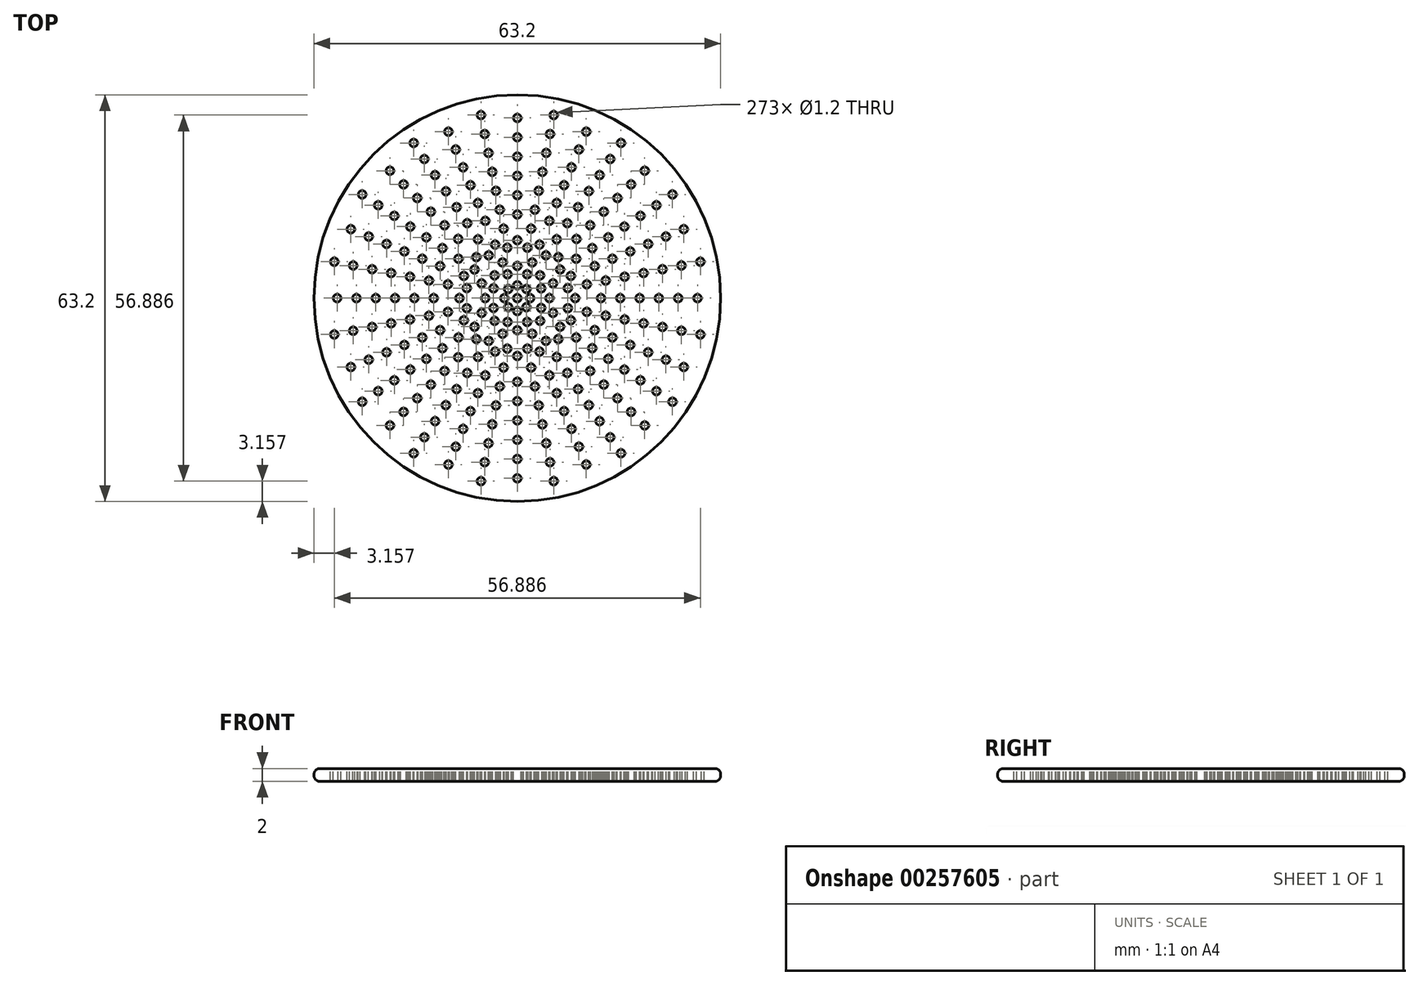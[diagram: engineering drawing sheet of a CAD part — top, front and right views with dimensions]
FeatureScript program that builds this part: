
annotation { "Feature Type Name" : "Feature", "Feature Type Description" : "" }
export const myFeature = defineFeature(function(context is Context, id is Id, definition is map)
    precondition{}
    {
        {
            var Q0;
            Q0=qCreatedBy(makeId("Front.planeOp"),FACE);
            var sketch = newSketch(context, id + "F0", { "sketchPlane" : qUnion([Q0])});
            skLineSegment(sketch, "E0", {"start": v(0, 0) * mm, "end": v(31.6, 0) * mm});
            skLineSegment(sketch, "E1", {"start": v(31.6, 0) * mm, "end": v(31.6, 2) * mm});
            skLineSegment(sketch, "E2", {"start": v(31.6, 2) * mm, "end": v(0, 2) * mm});
            skLineSegment(sketch, "E3", {"start": v(0, 2) * mm, "end": v(0, 0) * mm});
            skLineSegment(sketch, "E4", {"start": v(0, -1.67) * mm, "end": v(0, 4.38) * mm, "construction": true});
            skSolve(sketch);
        }
        {
            var Q0;
            Q0=makeQuery(id+"F0.imprint","IMPRINT",FACE,{"disambiguationData":[TD([[makeQuery(id+"F0.imprint","IMPRINT",EDGE,{"derivedFrom":sQuery(id+"F0.wireOp",EDGE,"E0")}),1.0]])]});
            var Q1;
            Q1=sQuery(id+"F0.wireOp",EDGE,"E4");
            revolve(context, id + "F1", {"entities" : qUnion([Q0]), "axis" : qUnion([Q1]), "revolveType" : RevolveType.FULL});
        }
        {
            var Q0;
            Q0=makeQuery(id+"F1.opRevolve","SWEPT_FACE",FACE,{"disambiguationData":[OSD([sQuery(id+"F0.wireOp",EDGE,"E2")])]});
            var sketch = newSketch(context, id + "F2", { "sketchPlane" : qUnion([Q0])});
            skCircle(sketch, "E5", {"center": v(0, 0) * mm, "radius": 2 * mm});
            skCircle(sketch, "E6", {"center": v(0, 0) * mm, "radius": 3 * mm});
            skCircle(sketch, "E7", {"center": v(0, 0) * mm, "radius": 4 * mm});
            skCircle(sketch, "E8", {"center": v(0, 0) * mm, "radius": 5 * mm});
            skCircle(sketch, "E9", {"center": v(0, 0) * mm, "radius": 6 * mm});
            skCircle(sketch, "E10", {"center": v(0, 0) * mm, "radius": 7 * mm});
            skCircle(sketch, "E11", {"center": v(0, 0) * mm, "radius": 8 * mm});
            skCircle(sketch, "E12", {"center": v(0, 0) * mm, "radius": 9 * mm});
            skCircle(sketch, "E13", {"center": v(0, 0) * mm, "radius": 10 * mm});
            skCircle(sketch, "E14", {"center": v(0, 0) * mm, "radius": 11 * mm});
            skCircle(sketch, "E15", {"center": v(0, 0) * mm, "radius": 12 * mm});
            skCircle(sketch, "E16", {"center": v(0, 0) * mm, "radius": 13 * mm});
            skCircle(sketch, "E17", {"center": v(0, 0) * mm, "radius": 14 * mm});
            skCircle(sketch, "E18", {"center": v(0, 0) * mm, "radius": 15 * mm});
            skCircle(sketch, "E19", {"center": v(0, 0) * mm, "radius": 16 * mm});
            skCircle(sketch, "E20", {"center": v(0, 0) * mm, "radius": 17 * mm});
            skCircle(sketch, "E21", {"center": v(0, 0) * mm, "radius": 18 * mm});
            skCircle(sketch, "E22", {"center": v(0, 0) * mm, "radius": 19 * mm});
            skCircle(sketch, "E23", {"center": v(0, 0) * mm, "radius": 20 * mm});
            skCircle(sketch, "E24", {"center": v(0, 0) * mm, "radius": 21 * mm});
            skCircle(sketch, "E25", {"center": v(0, 0) * mm, "radius": 23 * mm});
            skCircle(sketch, "E26", {"center": v(0, 0) * mm, "radius": 24 * mm});
            skCircle(sketch, "E27", {"center": v(0, 0) * mm, "radius": 22 * mm});
            skCircle(sketch, "E28", {"center": v(0, 0) * mm, "radius": 25 * mm});
            skCircle(sketch, "E29", {"center": v(0, 0) * mm, "radius": 26 * mm});
            skCircle(sketch, "E30", {"center": v(0, 0) * mm, "radius": 27 * mm});
            skCircle(sketch, "E31", {"center": v(0, 0) * mm, "radius": 28 * mm});
            skCircle(sketch, "E32", {"center": v(0, 0) * mm, "radius": 29 * mm});
            skLineSegment(sketch, "E33", {"start": v(0, 29) * mm, "end": v(0, -29) * mm});
            skLineSegment(sketch, "E34", {"start": v(-29, 0) * mm, "end": v(29, 0) * mm});
            skLineSegment(sketch, "E35", {"start": v(20.5, 20.5) * mm, "end": v(0, 0) * mm});
            skLineSegment(sketch, "E36", {"start": v(20.5, -20.5) * mm, "end": v(0, 0) * mm});
            skLineSegment(sketch, "E37", {"start": v(-20.5, -20.5) * mm, "end": v(0, 0) * mm});
            skLineSegment(sketch, "E38", {"start": v(-20.5, 20.5) * mm, "end": v(0, 0) * mm});
            skLineSegment(sketch, "E39", {"start": v(0, 0) * mm, "end": v(26.8, 11.1) * mm});
            skLineSegment(sketch, "E40", {"start": v(0, 0) * mm, "end": v(26.8, -11.1) * mm});
            skLineSegment(sketch, "E41", {"start": v(0, 0) * mm, "end": v(11.1, -26.8) * mm});
            skLineSegment(sketch, "E42", {"start": v(0, 0) * mm, "end": v(-11.1, -26.8) * mm});
            skLineSegment(sketch, "E43", {"start": v(0, 0) * mm, "end": v(-26.8, -11.1) * mm});
            skLineSegment(sketch, "E44", {"start": v(0, 0) * mm, "end": v(-26.8, 11.1) * mm});
            skLineSegment(sketch, "E45", {"start": v(0, 0) * mm, "end": v(-11.1, 26.8) * mm});
            skLineSegment(sketch, "E46", {"start": v(0, 0) * mm, "end": v(11.1, 26.8) * mm});
            skLineSegment(sketch, "E47", {"start": v(0, 0) * mm, "end": v(28.44, 5.66) * mm});
            skLineSegment(sketch, "E48", {"start": v(0, 0) * mm, "end": v(28.44, -5.66) * mm});
            skLineSegment(sketch, "E49", {"start": v(0, 0) * mm, "end": v(24.11, -16.11) * mm});
            skLineSegment(sketch, "E50", {"start": v(0, 0) * mm, "end": v(16.11, -24.11) * mm});
            skLineSegment(sketch, "E51", {"start": v(0, 0) * mm, "end": v(5.66, -28.44) * mm});
            skLineSegment(sketch, "E52", {"start": v(0, 0) * mm, "end": v(-5.66, -28.44) * mm});
            skLineSegment(sketch, "E53", {"start": v(0, 0) * mm, "end": v(-16.11, -24.11) * mm});
            skLineSegment(sketch, "E54", {"start": v(0, 0) * mm, "end": v(-24.11, -16.11) * mm});
            skLineSegment(sketch, "E55", {"start": v(0, 0) * mm, "end": v(-28.44, -5.66) * mm});
            skLineSegment(sketch, "E56", {"start": v(0, 0) * mm, "end": v(-28.44, 5.66) * mm});
            skLineSegment(sketch, "E57", {"start": v(0, 0) * mm, "end": v(-24.11, 16.11) * mm});
            skLineSegment(sketch, "E58", {"start": v(0, 0) * mm, "end": v(-16.11, 24.11) * mm});
            skLineSegment(sketch, "E59", {"start": v(0, 0) * mm, "end": v(-5.66, 28.44) * mm});
            skLineSegment(sketch, "E60", {"start": v(0, 0) * mm, "end": v(5.66, 28.44) * mm});
            skLineSegment(sketch, "E61", {"start": v(0, 0) * mm, "end": v(16.11, 24.11) * mm});
            skLineSegment(sketch, "E62", {"start": v(0, 0) * mm, "end": v(24.11, 16.11) * mm});
            skPoint(sketch, "E63", {"position": v(0, -2) * mm});
            skPoint(sketch, "E64", {"position": v(0, -3) * mm});
            skPoint(sketch, "E65", {"position": v(0, -4) * mm});
            skPoint(sketch, "E66", {"position": v(0, -5) * mm});
            skPoint(sketch, "E67", {"position": v(0, -6) * mm});
            skPoint(sketch, "E68", {"position": v(0, -7) * mm});
            skPoint(sketch, "E69", {"position": v(0, 2) * mm});
            skPoint(sketch, "E70", {"position": v(0, 3) * mm});
            skPoint(sketch, "E71", {"position": v(0.59, 2.94) * mm});
            skPoint(sketch, "E72", {"position": v(1.15, 2.77) * mm});
            skPoint(sketch, "E73", {"position": v(1.67, 2.5) * mm});
            skPoint(sketch, "E74", {"position": v(2.12, 2.12) * mm});
            skPoint(sketch, "E75", {"position": v(2.5, 1.67) * mm});
            skPoint(sketch, "E76", {"position": v(2.77, 1.15) * mm});
            skPoint(sketch, "E77", {"position": v(2.94, 0.59) * mm});
            skPoint(sketch, "E78", {"position": v(3, 0) * mm});
            skPoint(sketch, "E79", {"position": v(2.94, -0.59) * mm});
            skPoint(sketch, "E80", {"position": v(2.77, -1.15) * mm});
            skPoint(sketch, "E81", {"position": v(2.5, -1.67) * mm});
            skPoint(sketch, "E82", {"position": v(2.12, -2.12) * mm});
            skPoint(sketch, "E83", {"position": v(1.67, -2.5) * mm});
            skPoint(sketch, "E84", {"position": v(1.15, -2.77) * mm});
            skPoint(sketch, "E85", {"position": v(0.59, -2.94) * mm});
            skPoint(sketch, "E86", {"position": v(-0.59, -2.94) * mm});
            skPoint(sketch, "E87", {"position": v(-1.15, -2.77) * mm});
            skPoint(sketch, "E88", {"position": v(-1.67, -2.5) * mm});
            skPoint(sketch, "E89", {"position": v(-2.12, -2.12) * mm});
            skPoint(sketch, "E90", {"position": v(-2.5, -1.67) * mm});
            skPoint(sketch, "E91", {"position": v(-2.77, -1.15) * mm});
            skPoint(sketch, "E92", {"position": v(-2.94, -0.59) * mm});
            skPoint(sketch, "E93", {"position": v(-3, 0) * mm});
            skPoint(sketch, "E94", {"position": v(-2.94, 0.59) * mm});
            skPoint(sketch, "E95", {"position": v(-2.77, 1.15) * mm});
            skPoint(sketch, "E96", {"position": v(-2.5, 1.67) * mm});
            skPoint(sketch, "E97", {"position": v(-2.12, 2.12) * mm});
            skPoint(sketch, "E98", {"position": v(-1.67, 2.5) * mm});
            skPoint(sketch, "E99", {"position": v(-1.15, 2.77) * mm});
            skPoint(sketch, "E100", {"position": v(-0.59, 2.94) * mm});
            skPoint(sketch, "E101", {"position": v(-0.78, 3.92) * mm});
            skPoint(sketch, "E102", {"position": v(0, 4) * mm});
            skPoint(sketch, "E103", {"position": v(0.78, 3.92) * mm});
            skPoint(sketch, "E104", {"position": v(1.53, 3.7) * mm});
            skPoint(sketch, "E105", {"position": v(2.22, 3.33) * mm});
            skPoint(sketch, "E106", {"position": v(2.83, 2.83) * mm});
            skPoint(sketch, "E107", {"position": v(3.33, 2.22) * mm});
            skPoint(sketch, "E108", {"position": v(3.7, 1.53) * mm});
            skPoint(sketch, "E109", {"position": v(3.92, 0.78) * mm});
            skPoint(sketch, "E110", {"position": v(4, 0) * mm});
            skPoint(sketch, "E111", {"position": v(3.92, -0.78) * mm});
            skPoint(sketch, "E112", {"position": v(3.7, -1.53) * mm});
            skPoint(sketch, "E113", {"position": v(3.33, -2.22) * mm});
            skPoint(sketch, "E114", {"position": v(2.83, -2.83) * mm});
            skPoint(sketch, "E115", {"position": v(2.22, -3.33) * mm});
            skPoint(sketch, "E116", {"position": v(1.53, -3.7) * mm});
            skPoint(sketch, "E117", {"position": v(0.78, -3.92) * mm});
            skPoint(sketch, "E118", {"position": v(-0.78, -3.92) * mm});
            skPoint(sketch, "E119", {"position": v(-1.53, -3.7) * mm});
            skPoint(sketch, "E120", {"position": v(-2.22, -3.33) * mm});
            skPoint(sketch, "E121", {"position": v(-2.83, -2.83) * mm});
            skPoint(sketch, "E122", {"position": v(-3.33, -2.22) * mm});
            skPoint(sketch, "E123", {"position": v(-3.7, -1.53) * mm});
            skPoint(sketch, "E124", {"position": v(-3.92, -0.78) * mm});
            skPoint(sketch, "E125", {"position": v(-4, 0) * mm});
            skPoint(sketch, "E126", {"position": v(-3.92, 0.78) * mm});
            skPoint(sketch, "E127", {"position": v(-3.7, 1.53) * mm});
            skPoint(sketch, "E128", {"position": v(-3.33, 2.22) * mm});
            skPoint(sketch, "E129", {"position": v(-2.83, 2.83) * mm});
            skPoint(sketch, "E130", {"position": v(-2.22, 3.33) * mm});
            skPoint(sketch, "E131", {"position": v(-1.53, 3.7) * mm});
            skPoint(sketch, "E132", {"position": v(-0.98, 4.9) * mm});
            skPoint(sketch, "E133", {"position": v(0, 5) * mm});
            skPoint(sketch, "E134", {"position": v(0.98, 4.9) * mm});
            skPoint(sketch, "E135", {"position": v(2.78, 4.16) * mm});
            skPoint(sketch, "E136", {"position": v(1.91, 4.62) * mm});
            skPoint(sketch, "E137", {"position": v(3.54, 3.54) * mm});
            skPoint(sketch, "E138", {"position": v(4.16, 2.78) * mm});
            skPoint(sketch, "E139", {"position": v(4.62, 1.91) * mm});
            skPoint(sketch, "E140", {"position": v(4.9, 0.98) * mm});
            skPoint(sketch, "E141", {"position": v(5, 0) * mm});
            skPoint(sketch, "E142", {"position": v(4.9, -0.98) * mm});
            skPoint(sketch, "E143", {"position": v(4.62, -1.91) * mm});
            skPoint(sketch, "E144", {"position": v(4.16, -2.78) * mm});
            skPoint(sketch, "E145", {"position": v(3.54, -3.54) * mm});
            skPoint(sketch, "E146", {"position": v(2.78, -4.16) * mm});
            skPoint(sketch, "E147", {"position": v(1.91, -4.62) * mm});
            skPoint(sketch, "E148", {"position": v(0.98, -4.9) * mm});
            skPoint(sketch, "E149", {"position": v(-0.98, -4.9) * mm});
            skPoint(sketch, "E150", {"position": v(-1.91, -4.62) * mm});
            skPoint(sketch, "E151", {"position": v(-2.78, -4.16) * mm});
            skPoint(sketch, "E152", {"position": v(-3.54, -3.54) * mm});
            skPoint(sketch, "E153", {"position": v(-4.16, -2.78) * mm});
            skPoint(sketch, "E154", {"position": v(-4.62, -1.91) * mm});
            skPoint(sketch, "E155", {"position": v(-4.9, -0.98) * mm});
            skPoint(sketch, "E156", {"position": v(-5, 0) * mm});
            skPoint(sketch, "E157", {"position": v(-4.9, 0.98) * mm});
            skPoint(sketch, "E158", {"position": v(-4.62, 1.91) * mm});
            skPoint(sketch, "E159", {"position": v(-4.16, 2.78) * mm});
            skPoint(sketch, "E160", {"position": v(-3.54, 3.54) * mm});
            skPoint(sketch, "E161", {"position": v(-2.78, 4.16) * mm});
            skPoint(sketch, "E162", {"position": v(-1.91, 4.62) * mm});
            skPoint(sketch, "E163", {"position": v(0, 6) * mm});
            skPoint(sketch, "E164", {"position": v(0, 7) * mm});
            skPoint(sketch, "E165", {"position": v(0, 8) * mm});
            skPoint(sketch, "E166", {"position": v(0, 9) * mm});
            skPoint(sketch, "E167", {"position": v(0, 10) * mm});
            skPoint(sketch, "E168", {"position": v(0, 11) * mm});
            skPoint(sketch, "E169", {"position": v(0, 12) * mm});
            skPoint(sketch, "E170", {"position": v(0, 13) * mm});
            skPoint(sketch, "E171", {"position": v(0, 14) * mm});
            skPoint(sketch, "E172", {"position": v(0, 15) * mm});
            skPoint(sketch, "E173", {"position": v(0, 16) * mm});
            skPoint(sketch, "E174", {"position": v(0, 17) * mm});
            skPoint(sketch, "E175", {"position": v(0, 18) * mm});
            skPoint(sketch, "E176", {"position": v(1.17, 5.88) * mm});
            skPoint(sketch, "E177", {"position": v(2.3, 5.54) * mm});
            skPoint(sketch, "E178", {"position": v(3.33, 4.99) * mm});
            skPoint(sketch, "E179", {"position": v(4.24, 4.24) * mm});
            skPoint(sketch, "E180", {"position": v(4.99, 3.33) * mm});
            skPoint(sketch, "E181", {"position": v(5.54, 2.3) * mm});
            skPoint(sketch, "E182", {"position": v(5.88, 1.17) * mm});
            skPoint(sketch, "E183", {"position": v(6, 0) * mm});
            skPoint(sketch, "E184", {"position": v(5.88, -1.17) * mm});
            skPoint(sketch, "E185", {"position": v(5.54, -2.3) * mm});
            skPoint(sketch, "E186", {"position": v(4.99, -3.33) * mm});
            skPoint(sketch, "E187", {"position": v(4.24, -4.24) * mm});
            skPoint(sketch, "E188", {"position": v(3.33, -4.99) * mm});
            skPoint(sketch, "E189", {"position": v(2.3, -5.54) * mm});
            skPoint(sketch, "E190", {"position": v(1.17, -5.88) * mm});
            skPoint(sketch, "E191", {"position": v(-1.17, -5.88) * mm});
            skPoint(sketch, "E192", {"position": v(-2.3, -5.54) * mm});
            skPoint(sketch, "E193", {"position": v(-3.33, -4.99) * mm});
            skPoint(sketch, "E194", {"position": v(-4.24, -4.24) * mm});
            skPoint(sketch, "E195", {"position": v(-4.99, -3.33) * mm});
            skPoint(sketch, "E196", {"position": v(-5.54, -2.3) * mm});
            skPoint(sketch, "E197", {"position": v(-5.88, -1.17) * mm});
            skPoint(sketch, "E198", {"position": v(-6, 0) * mm});
            skPoint(sketch, "E199", {"position": v(-5.88, 1.17) * mm});
            skPoint(sketch, "E200", {"position": v(-5.54, 2.3) * mm});
            skPoint(sketch, "E201", {"position": v(-4.99, 3.33) * mm});
            skPoint(sketch, "E202", {"position": v(-4.24, 4.24) * mm});
            skPoint(sketch, "E203", {"position": v(-3.33, 4.99) * mm});
            skPoint(sketch, "E204", {"position": v(-2.3, 5.54) * mm});
            skPoint(sketch, "E205", {"position": v(-1.17, 5.88) * mm});
            skPoint(sketch, "E206", {"position": v(-1.37, 6.87) * mm});
            skPoint(sketch, "E207", {"position": v(1.37, 6.87) * mm});
            skPoint(sketch, "E208", {"position": v(2.68, 6.47) * mm});
            skPoint(sketch, "E209", {"position": v(3.89, 5.82) * mm});
            skPoint(sketch, "E210", {"position": v(4.95, 4.95) * mm});
            skPoint(sketch, "E211", {"position": v(5.82, 3.89) * mm});
            skPoint(sketch, "E212", {"position": v(6.47, 2.68) * mm});
            skPoint(sketch, "E213", {"position": v(6.87, 1.37) * mm});
            skPoint(sketch, "E214", {"position": v(7, 0) * mm});
            skPoint(sketch, "E215", {"position": v(6.87, -1.37) * mm});
            skPoint(sketch, "E216", {"position": v(6.47, -2.68) * mm});
            skPoint(sketch, "E217", {"position": v(5.82, -3.89) * mm});
            skPoint(sketch, "E218", {"position": v(4.95, -4.95) * mm});
            skPoint(sketch, "E219", {"position": v(3.89, -5.82) * mm});
            skPoint(sketch, "E220", {"position": v(2.68, -6.47) * mm});
            skPoint(sketch, "E221", {"position": v(1.37, -6.87) * mm});
            skPoint(sketch, "E222", {"position": v(-1.37, -6.87) * mm});
            skPoint(sketch, "E223", {"position": v(-2.68, -6.47) * mm});
            skPoint(sketch, "E224", {"position": v(-3.89, -5.82) * mm});
            skPoint(sketch, "E225", {"position": v(-4.95, -4.95) * mm});
            skPoint(sketch, "E226", {"position": v(-5.82, -3.89) * mm});
            skPoint(sketch, "E227", {"position": v(-6.47, -2.68) * mm});
            skPoint(sketch, "E228", {"position": v(-6.87, -1.37) * mm});
            skPoint(sketch, "E229", {"position": v(-7, 0) * mm});
            skPoint(sketch, "E230", {"position": v(-6.87, 1.37) * mm});
            skPoint(sketch, "E231", {"position": v(-6.47, 2.68) * mm});
            skPoint(sketch, "E232", {"position": v(-5.82, 3.89) * mm});
            skPoint(sketch, "E233", {"position": v(-4.95, 4.95) * mm});
            skPoint(sketch, "E234", {"position": v(-3.89, 5.82) * mm});
            skPoint(sketch, "E235", {"position": v(-2.68, 6.47) * mm});
            skPoint(sketch, "E236", {"position": v(-1.56, 7.85) * mm});
            skPoint(sketch, "E237", {"position": v(1.56, 7.85) * mm});
            skPoint(sketch, "E238", {"position": v(3.06, 7.4) * mm});
            skPoint(sketch, "E239", {"position": v(4.44, 6.65) * mm});
            skPoint(sketch, "E240", {"position": v(5.66, 5.66) * mm});
            skPoint(sketch, "E241", {"position": v(6.65, 4.44) * mm});
            skPoint(sketch, "E242", {"position": v(7.4, 3.06) * mm});
            skPoint(sketch, "E243", {"position": v(7.85, 1.56) * mm});
            skPoint(sketch, "E244", {"position": v(8, 0) * mm});
            skPoint(sketch, "E245", {"position": v(7.85, -1.56) * mm});
            skPoint(sketch, "E246", {"position": v(7.4, -3.06) * mm});
            skPoint(sketch, "E247", {"position": v(6.65, -4.44) * mm});
            skPoint(sketch, "E248", {"position": v(5.66, -5.66) * mm});
            skPoint(sketch, "E249", {"position": v(4.44, -6.65) * mm});
            skPoint(sketch, "E250", {"position": v(3.06, -7.4) * mm});
            skPoint(sketch, "E251", {"position": v(1.56, -7.85) * mm});
            skPoint(sketch, "E252", {"position": v(0, -8) * mm});
            skPoint(sketch, "E253", {"position": v(-1.56, -7.85) * mm});
            skPoint(sketch, "E254", {"position": v(-3.06, -7.4) * mm});
            skPoint(sketch, "E255", {"position": v(-4.44, -6.65) * mm});
            skPoint(sketch, "E256", {"position": v(-5.66, -5.66) * mm});
            skPoint(sketch, "E257", {"position": v(-6.65, -4.44) * mm});
            skPoint(sketch, "E258", {"position": v(-7.4, -3.06) * mm});
            skPoint(sketch, "E259", {"position": v(-7.85, -1.56) * mm});
            skPoint(sketch, "E260", {"position": v(-8, 0) * mm});
            skPoint(sketch, "E261", {"position": v(-7.85, 1.56) * mm});
            skPoint(sketch, "E262", {"position": v(-7.4, 3.06) * mm});
            skPoint(sketch, "E263", {"position": v(-6.65, 4.44) * mm});
            skPoint(sketch, "E264", {"position": v(-5.66, 5.66) * mm});
            skPoint(sketch, "E265", {"position": v(-4.44, 6.65) * mm});
            skPoint(sketch, "E266", {"position": v(-3.06, 7.4) * mm});
            skPoint(sketch, "E267", {"position": v(-1.76, 8.83) * mm});
            skPoint(sketch, "E268", {"position": v(1.76, 8.83) * mm});
            skPoint(sketch, "E269", {"position": v(3.44, 8.31) * mm});
            skPoint(sketch, "E270", {"position": v(5, 7.48) * mm});
            skPoint(sketch, "E271", {"position": v(6.36, 6.36) * mm});
            skPoint(sketch, "E272", {"position": v(7.48, 5) * mm});
            skPoint(sketch, "E273", {"position": v(8.31, 3.44) * mm});
            skPoint(sketch, "E274", {"position": v(8.83, 1.76) * mm});
            skPoint(sketch, "E275", {"position": v(9, 0) * mm});
            skPoint(sketch, "E276", {"position": v(8.83, -1.76) * mm});
            skPoint(sketch, "E277", {"position": v(8.31, -3.44) * mm});
            skPoint(sketch, "E278", {"position": v(7.48, -5) * mm});
            skPoint(sketch, "E279", {"position": v(6.36, -6.36) * mm});
            skPoint(sketch, "E280", {"position": v(5, -7.48) * mm});
            skPoint(sketch, "E281", {"position": v(3.44, -8.31) * mm});
            skPoint(sketch, "E282", {"position": v(1.76, -8.83) * mm});
            skPoint(sketch, "E283", {"position": v(0, -9) * mm});
            skPoint(sketch, "E284", {"position": v(-1.76, -8.83) * mm});
            skPoint(sketch, "E285", {"position": v(-3.44, -8.31) * mm});
            skPoint(sketch, "E286", {"position": v(-5, -7.48) * mm});
            skPoint(sketch, "E287", {"position": v(-6.36, -6.36) * mm});
            skPoint(sketch, "E288", {"position": v(-7.48, -5) * mm});
            skPoint(sketch, "E289", {"position": v(-8.31, -3.44) * mm});
            skPoint(sketch, "E290", {"position": v(-8.83, -1.76) * mm});
            skPoint(sketch, "E291", {"position": v(-9, 0) * mm});
            skPoint(sketch, "E292", {"position": v(-8.83, 1.76) * mm});
            skPoint(sketch, "E293", {"position": v(-8.31, 3.44) * mm});
            skPoint(sketch, "E294", {"position": v(-7.48, 5) * mm});
            skPoint(sketch, "E295", {"position": v(-6.36, 6.36) * mm});
            skPoint(sketch, "E296", {"position": v(-5, 7.48) * mm});
            skPoint(sketch, "E297", {"position": v(-3.44, 8.31) * mm});
            skPoint(sketch, "E298", {"position": v(-1.95, 9.8) * mm});
            skPoint(sketch, "E299", {"position": v(1.95, 9.8) * mm});
            skPoint(sketch, "E300", {"position": v(3.83, 9.24) * mm});
            skPoint(sketch, "E301", {"position": v(5.56, 8.31) * mm});
            skPoint(sketch, "E302", {"position": v(7.07, 7.07) * mm});
            skPoint(sketch, "E303", {"position": v(8.31, 5.56) * mm});
            skPoint(sketch, "E304", {"position": v(9.24, 3.83) * mm});
            skPoint(sketch, "E305", {"position": v(9.8, 1.95) * mm});
            skPoint(sketch, "E306", {"position": v(10, 0) * mm});
            skPoint(sketch, "E307", {"position": v(9.8, -1.95) * mm});
            skPoint(sketch, "E308", {"position": v(9.24, -3.83) * mm});
            skPoint(sketch, "E309", {"position": v(8.31, -5.56) * mm});
            skPoint(sketch, "E310", {"position": v(7.07, -7.07) * mm});
            skPoint(sketch, "E311", {"position": v(5.56, -8.31) * mm});
            skPoint(sketch, "E312", {"position": v(3.83, -9.24) * mm});
            skPoint(sketch, "E313", {"position": v(1.95, -9.8) * mm});
            skPoint(sketch, "E314", {"position": v(0, -10) * mm});
            skPoint(sketch, "E315", {"position": v(-1.95, -9.8) * mm});
            skPoint(sketch, "E316", {"position": v(-3.83, -9.24) * mm});
            skPoint(sketch, "E317", {"position": v(-5.56, -8.31) * mm});
            skPoint(sketch, "E318", {"position": v(-7.07, -7.07) * mm});
            skPoint(sketch, "E319", {"position": v(-8.31, -5.56) * mm});
            skPoint(sketch, "E320", {"position": v(-9.24, -3.83) * mm});
            skPoint(sketch, "E321", {"position": v(-9.8, -1.95) * mm});
            skPoint(sketch, "E322", {"position": v(-10, 0) * mm});
            skPoint(sketch, "E323", {"position": v(-9.8, 1.95) * mm});
            skPoint(sketch, "E324", {"position": v(-9.24, 3.83) * mm});
            skPoint(sketch, "E325", {"position": v(-8.31, 5.56) * mm});
            skPoint(sketch, "E326", {"position": v(-7.07, 7.07) * mm});
            skPoint(sketch, "E327", {"position": v(-5.56, 8.31) * mm});
            skPoint(sketch, "E328", {"position": v(-3.83, 9.24) * mm});
            skPoint(sketch, "E329", {"position": v(-2.15, 10.79) * mm});
            skPoint(sketch, "E330", {"position": v(2.15, 10.79) * mm});
            skPoint(sketch, "E331", {"position": v(4.2, 10.16) * mm});
            skPoint(sketch, "E332", {"position": v(6.11, 9.15) * mm});
            skPoint(sketch, "E333", {"position": v(7.78, 7.78) * mm});
            skPoint(sketch, "E334", {"position": v(9.15, 6.11) * mm});
            skPoint(sketch, "E335", {"position": v(10.16, 4.2) * mm});
            skPoint(sketch, "E336", {"position": v(10.79, 2.15) * mm});
            skPoint(sketch, "E337", {"position": v(11, 0) * mm});
            skPoint(sketch, "E338", {"position": v(10.79, -2.15) * mm});
            skPoint(sketch, "E339", {"position": v(10.16, -4.2) * mm});
            skPoint(sketch, "E340", {"position": v(9.15, -6.11) * mm});
            skPoint(sketch, "E341", {"position": v(7.78, -7.78) * mm});
            skPoint(sketch, "E342", {"position": v(6.11, -9.15) * mm});
            skPoint(sketch, "E343", {"position": v(4.2, -10.16) * mm});
            skPoint(sketch, "E344", {"position": v(2.15, -10.79) * mm});
            skPoint(sketch, "E345", {"position": v(0, -11) * mm});
            skPoint(sketch, "E346", {"position": v(-2.15, -10.79) * mm});
            skPoint(sketch, "E347", {"position": v(-4.2, -10.16) * mm});
            skPoint(sketch, "E348", {"position": v(-6.11, -9.15) * mm});
            skPoint(sketch, "E349", {"position": v(-7.78, -7.78) * mm});
            skPoint(sketch, "E350", {"position": v(-9.15, -6.11) * mm});
            skPoint(sketch, "E351", {"position": v(-10.16, -4.2) * mm});
            skPoint(sketch, "E352", {"position": v(-10.79, -2.15) * mm});
            skPoint(sketch, "E353", {"position": v(-11, 0) * mm});
            skPoint(sketch, "E354", {"position": v(-10.79, 2.15) * mm});
            skPoint(sketch, "E355", {"position": v(-10.16, 4.2) * mm});
            skPoint(sketch, "E356", {"position": v(-9.15, 6.11) * mm});
            skPoint(sketch, "E357", {"position": v(-7.78, 7.78) * mm});
            skPoint(sketch, "E358", {"position": v(-6.11, 9.15) * mm});
            skPoint(sketch, "E359", {"position": v(-4.2, 10.16) * mm});
            skPoint(sketch, "E360", {"position": v(2.34, 11.77) * mm});
            skPoint(sketch, "E361", {"position": v(4.6, 11.09) * mm});
            skPoint(sketch, "E362", {"position": v(6.67, 9.98) * mm});
            skPoint(sketch, "E363", {"position": v(8.49, 8.49) * mm});
            skPoint(sketch, "E364", {"position": v(9.98, 6.67) * mm});
            skPoint(sketch, "E365", {"position": v(11.09, 4.6) * mm});
            skPoint(sketch, "E366", {"position": v(11.77, 2.34) * mm});
            skPoint(sketch, "E367", {"position": v(12, 0) * mm});
            skPoint(sketch, "E368", {"position": v(11.77, -2.34) * mm});
            skPoint(sketch, "E369", {"position": v(11.09, -4.6) * mm});
            skPoint(sketch, "E370", {"position": v(9.98, -6.67) * mm});
            skPoint(sketch, "E371", {"position": v(8.49, -8.49) * mm});
            skPoint(sketch, "E372", {"position": v(6.67, -9.98) * mm});
            skPoint(sketch, "E373", {"position": v(4.6, -11.09) * mm});
            skPoint(sketch, "E374", {"position": v(2.34, -11.77) * mm});
            skPoint(sketch, "E375", {"position": v(0, -12) * mm});
            skPoint(sketch, "E376", {"position": v(-2.34, -11.77) * mm});
            skPoint(sketch, "E377", {"position": v(-4.6, -11.09) * mm});
            skPoint(sketch, "E378", {"position": v(-6.67, -9.98) * mm});
            skPoint(sketch, "E379", {"position": v(-8.49, -8.49) * mm});
            skPoint(sketch, "E380", {"position": v(-9.98, -6.67) * mm});
            skPoint(sketch, "E381", {"position": v(-11.09, -4.6) * mm});
            skPoint(sketch, "E382", {"position": v(-11.77, -2.34) * mm});
            skPoint(sketch, "E383", {"position": v(-12, 0) * mm});
            skPoint(sketch, "E384", {"position": v(-29, 0) * mm});
            skPoint(sketch, "E385", {"position": v(-28, 0) * mm});
            skPoint(sketch, "E386", {"position": v(-27, 0) * mm});
            skPoint(sketch, "E387", {"position": v(-26, 0) * mm});
            skPoint(sketch, "E388", {"position": v(-25, 0) * mm});
            skPoint(sketch, "E389", {"position": v(-24, 0) * mm});
            skPoint(sketch, "E390", {"position": v(-23, 0) * mm});
            skPoint(sketch, "E391", {"position": v(-22, 0) * mm});
            skPoint(sketch, "E392", {"position": v(-21, 0) * mm});
            skPoint(sketch, "E393", {"position": v(-20, 0) * mm});
            skPoint(sketch, "E394", {"position": v(-19, 0) * mm});
            skPoint(sketch, "E395", {"position": v(-18, 0) * mm});
            skPoint(sketch, "E396", {"position": v(-17, 0) * mm});
            skPoint(sketch, "E397", {"position": v(-16, 0) * mm});
            skPoint(sketch, "E398", {"position": v(-15, 0) * mm});
            skPoint(sketch, "E399", {"position": v(-14, 0) * mm});
            skPoint(sketch, "E400", {"position": v(-13, 0) * mm});
            skPoint(sketch, "E401", {"position": v(-28.44, 5.66) * mm});
            skPoint(sketch, "E402", {"position": v(-27.46, 5.46) * mm});
            skPoint(sketch, "E403", {"position": v(-26.48, 5.27) * mm});
            skPoint(sketch, "E404", {"position": v(-25.5, 5.07) * mm});
            skPoint(sketch, "E405", {"position": v(-24.52, 4.88) * mm});
            skPoint(sketch, "E406", {"position": v(-23.54, 4.68) * mm});
            skPoint(sketch, "E407", {"position": v(-22.56, 4.49) * mm});
            skPoint(sketch, "E408", {"position": v(-21.58, 4.3) * mm});
            skPoint(sketch, "E409", {"position": v(-20.6, 4.1) * mm});
            skPoint(sketch, "E410", {"position": v(-19.62, 3.9) * mm});
            skPoint(sketch, "E411", {"position": v(-18.63, 3.7) * mm});
            skPoint(sketch, "E412", {"position": v(-17.65, 3.51) * mm});
            skPoint(sketch, "E413", {"position": v(-16.67, 3.32) * mm});
            skPoint(sketch, "E414", {"position": v(-15.7, 3.12) * mm});
            skPoint(sketch, "E415", {"position": v(-14.71, 2.93) * mm});
            skPoint(sketch, "E416", {"position": v(-13.73, 2.73) * mm});
            skPoint(sketch, "E417", {"position": v(-12.75, 2.54) * mm});
            skPoint(sketch, "E418", {"position": v(-11.77, 2.34) * mm});
            skPoint(sketch, "E419", {"position": v(-28.44, -5.66) * mm});
            skPoint(sketch, "E420", {"position": v(-27.46, -5.46) * mm});
            skPoint(sketch, "E421", {"position": v(-26.48, -5.27) * mm});
            skPoint(sketch, "E422", {"position": v(-25.5, -5.07) * mm});
            skPoint(sketch, "E423", {"position": v(-24.52, -4.88) * mm});
            skPoint(sketch, "E424", {"position": v(-23.54, -4.68) * mm});
            skPoint(sketch, "E425", {"position": v(-22.56, -4.49) * mm});
            skPoint(sketch, "E426", {"position": v(-21.58, -4.3) * mm});
            skPoint(sketch, "E427", {"position": v(-20.6, -4.1) * mm});
            skPoint(sketch, "E428", {"position": v(-19.62, -3.9) * mm});
            skPoint(sketch, "E429", {"position": v(-18.63, -3.7) * mm});
            skPoint(sketch, "E430", {"position": v(-17.65, -3.51) * mm});
            skPoint(sketch, "E431", {"position": v(-16.67, -3.32) * mm});
            skPoint(sketch, "E432", {"position": v(-15.7, -3.12) * mm});
            skPoint(sketch, "E433", {"position": v(-14.71, -2.93) * mm});
            skPoint(sketch, "E434", {"position": v(-13.73, -2.73) * mm});
            skPoint(sketch, "E435", {"position": v(-12.75, -2.54) * mm});
            skPoint(sketch, "E436", {"position": v(-12.01, -4.97) * mm});
            skPoint(sketch, "E437", {"position": v(-12.93, -5.36) * mm});
            skPoint(sketch, "E438", {"position": v(-13.86, -5.74) * mm});
            skPoint(sketch, "E439", {"position": v(-14.78, -6.12) * mm});
            skPoint(sketch, "E440", {"position": v(-15.7, -6.5) * mm});
            skPoint(sketch, "E441", {"position": v(-16.63, -6.89) * mm});
            skPoint(sketch, "E442", {"position": v(-17.55, -7.27) * mm});
            skPoint(sketch, "E443", {"position": v(-18.48, -7.65) * mm});
            skPoint(sketch, "E444", {"position": v(-19.4, -8.04) * mm});
            skPoint(sketch, "E445", {"position": v(-20.33, -8.42) * mm});
            skPoint(sketch, "E446", {"position": v(-21.25, -8.8) * mm});
            skPoint(sketch, "E447", {"position": v(-22.17, -9.18) * mm});
            skPoint(sketch, "E448", {"position": v(-23.1, -9.57) * mm});
            skPoint(sketch, "E449", {"position": v(-24.02, -9.95) * mm});
            skPoint(sketch, "E450", {"position": v(-24.94, -10.33) * mm});
            skPoint(sketch, "E451", {"position": v(-25.87, -10.72) * mm});
            skPoint(sketch, "E452", {"position": v(-26.8, -11.1) * mm});
            skPoint(sketch, "E453", {"position": v(-10.8, -7.22) * mm});
            skPoint(sketch, "E454", {"position": v(-11.64, -7.78) * mm});
            skPoint(sketch, "E455", {"position": v(-12.47, -8.33) * mm});
            skPoint(sketch, "E456", {"position": v(-13.3, -8.89) * mm});
            skPoint(sketch, "E457", {"position": v(-14.13, -9.44) * mm});
            skPoint(sketch, "E458", {"position": v(-14.97, -10) * mm});
            skPoint(sketch, "E459", {"position": v(-15.8, -10.56) * mm});
            skPoint(sketch, "E460", {"position": v(-16.63, -11.11) * mm});
            skPoint(sketch, "E461", {"position": v(-17.46, -11.67) * mm});
            skPoint(sketch, "E462", {"position": v(-18.3, -12.22) * mm});
            skPoint(sketch, "E463", {"position": v(-19.12, -12.78) * mm});
            skPoint(sketch, "E464", {"position": v(-19.96, -13.33) * mm});
            skPoint(sketch, "E465", {"position": v(-20.79, -13.89) * mm});
            skPoint(sketch, "E466", {"position": v(-21.62, -14.44) * mm});
            skPoint(sketch, "E467", {"position": v(-22.45, -15) * mm});
            skPoint(sketch, "E468", {"position": v(-23.28, -15.56) * mm});
            skPoint(sketch, "E469", {"position": v(-24.11, -16.11) * mm});
            skPoint(sketch, "E470", {"position": v(-9.2, -9.2) * mm});
            skPoint(sketch, "E471", {"position": v(-9.9, -9.9) * mm});
            skPoint(sketch, "E472", {"position": v(-10.6, -10.6) * mm});
            skPoint(sketch, "E473", {"position": v(-11.31, -11.31) * mm});
            skPoint(sketch, "E474", {"position": v(-12.02, -12.02) * mm});
            skPoint(sketch, "E475", {"position": v(-12.73, -12.73) * mm});
            skPoint(sketch, "E476", {"position": v(-13.44, -13.44) * mm});
            skPoint(sketch, "E477", {"position": v(-14.14, -14.14) * mm});
            skPoint(sketch, "E478", {"position": v(-14.85, -14.85) * mm});
            skPoint(sketch, "E479", {"position": v(-15.56, -15.56) * mm});
            skPoint(sketch, "E480", {"position": v(-16.26, -16.26) * mm});
            skPoint(sketch, "E481", {"position": v(-16.97, -16.97) * mm});
            skPoint(sketch, "E482", {"position": v(-17.68, -17.68) * mm});
            skPoint(sketch, "E483", {"position": v(-18.38, -18.38) * mm});
            skPoint(sketch, "E484", {"position": v(-19.1, -19.1) * mm});
            skPoint(sketch, "E485", {"position": v(-19.8, -19.8) * mm});
            skPoint(sketch, "E486", {"position": v(-20.5, -20.5) * mm});
            skPoint(sketch, "E487", {"position": v(-7.22, -10.8) * mm});
            skPoint(sketch, "E488", {"position": v(-7.78, -11.64) * mm});
            skPoint(sketch, "E489", {"position": v(-8.33, -12.47) * mm});
            skPoint(sketch, "E490", {"position": v(-8.89, -13.3) * mm});
            skPoint(sketch, "E491", {"position": v(-9.44, -14.13) * mm});
            skPoint(sketch, "E492", {"position": v(-10, -14.97) * mm});
            skPoint(sketch, "E493", {"position": v(-10.56, -15.8) * mm});
            skPoint(sketch, "E494", {"position": v(-11.11, -16.63) * mm});
            skPoint(sketch, "E495", {"position": v(-11.67, -17.46) * mm});
            skPoint(sketch, "E496", {"position": v(-12.22, -18.3) * mm});
            skPoint(sketch, "E497", {"position": v(-12.78, -19.12) * mm});
            skPoint(sketch, "E498", {"position": v(-13.33, -19.96) * mm});
            skPoint(sketch, "E499", {"position": v(-13.89, -20.79) * mm});
            skPoint(sketch, "E500", {"position": v(-14.44, -21.62) * mm});
            skPoint(sketch, "E501", {"position": v(-15, -22.45) * mm});
            skPoint(sketch, "E502", {"position": v(-15.56, -23.28) * mm});
            skPoint(sketch, "E503", {"position": v(-16.11, -24.11) * mm});
            skPoint(sketch, "E504", {"position": v(-11.1, -26.8) * mm});
            skPoint(sketch, "E505", {"position": v(-5.66, -28.44) * mm});
            skPoint(sketch, "E506", {"position": v(0, -29) * mm});
            skPoint(sketch, "E507", {"position": v(5.66, -28.44) * mm});
            skPoint(sketch, "E508", {"position": v(-10.72, -25.87) * mm});
            skPoint(sketch, "E509", {"position": v(-10.33, -24.94) * mm});
            skPoint(sketch, "E510", {"position": v(-9.95, -24.02) * mm});
            skPoint(sketch, "E511", {"position": v(-9.57, -23.1) * mm});
            skPoint(sketch, "E512", {"position": v(-9.18, -22.17) * mm});
            skPoint(sketch, "E513", {"position": v(-8.8, -21.25) * mm});
            skPoint(sketch, "E514", {"position": v(-8.42, -20.33) * mm});
            skPoint(sketch, "E515", {"position": v(-8.04, -19.4) * mm});
            skPoint(sketch, "E516", {"position": v(-7.65, -18.48) * mm});
            skPoint(sketch, "E517", {"position": v(-7.27, -17.55) * mm});
            skPoint(sketch, "E518", {"position": v(-6.89, -16.63) * mm});
            skPoint(sketch, "E519", {"position": v(-6.5, -15.7) * mm});
            skPoint(sketch, "E520", {"position": v(-6.12, -14.78) * mm});
            skPoint(sketch, "E521", {"position": v(-5.66, -13.66) * mm});
            skPoint(sketch, "E522", {"position": v(-5.36, -12.93) * mm});
            skPoint(sketch, "E523", {"position": v(-4.97, -12.01) * mm});
            skPoint(sketch, "E524", {"position": v(-2.54, -12.75) * mm});
            skPoint(sketch, "E525", {"position": v(-2.73, -13.73) * mm});
            skPoint(sketch, "E526", {"position": v(-2.93, -14.71) * mm});
            skPoint(sketch, "E527", {"position": v(-3.12, -15.7) * mm});
            skPoint(sketch, "E528", {"position": v(-3.32, -16.67) * mm});
            skPoint(sketch, "E529", {"position": v(-3.51, -17.65) * mm});
            skPoint(sketch, "E530", {"position": v(-3.7, -18.63) * mm});
            skPoint(sketch, "E531", {"position": v(-3.9, -19.62) * mm});
            skPoint(sketch, "E532", {"position": v(-4.1, -20.6) * mm});
            skPoint(sketch, "E533", {"position": v(-4.3, -21.58) * mm});
            skPoint(sketch, "E534", {"position": v(-4.49, -22.56) * mm});
            skPoint(sketch, "E535", {"position": v(-4.68, -23.54) * mm});
            skPoint(sketch, "E536", {"position": v(-4.88, -24.52) * mm});
            skPoint(sketch, "E537", {"position": v(-5.07, -25.5) * mm});
            skPoint(sketch, "E538", {"position": v(-5.27, -26.48) * mm});
            skPoint(sketch, "E539", {"position": v(-5.46, -27.46) * mm});
            skPoint(sketch, "E540", {"position": v(0, -13) * mm});
            skPoint(sketch, "E541", {"position": v(0, -14) * mm});
            skPoint(sketch, "E542", {"position": v(0, -15) * mm});
            skPoint(sketch, "E543", {"position": v(0, -16) * mm});
            skPoint(sketch, "E544", {"position": v(0, -17) * mm});
            skPoint(sketch, "E545", {"position": v(0, -18) * mm});
            skPoint(sketch, "E546", {"position": v(0, -19) * mm});
            skPoint(sketch, "E547", {"position": v(0, -20) * mm});
            skPoint(sketch, "E548", {"position": v(0, -21) * mm});
            skPoint(sketch, "E549", {"position": v(0, -22) * mm});
            skPoint(sketch, "E550", {"position": v(0, -23) * mm});
            skPoint(sketch, "E551", {"position": v(0, -24) * mm});
            skPoint(sketch, "E552", {"position": v(0, -25) * mm});
            skPoint(sketch, "E553", {"position": v(0, -26) * mm});
            skPoint(sketch, "E554", {"position": v(0, -27) * mm});
            skPoint(sketch, "E555", {"position": v(0, -28) * mm});
            skPoint(sketch, "E556", {"position": v(2.54, -12.75) * mm});
            skPoint(sketch, "E557", {"position": v(2.73, -13.73) * mm});
            skPoint(sketch, "E558", {"position": v(2.93, -14.71) * mm});
            skPoint(sketch, "E559", {"position": v(3.12, -15.7) * mm});
            skPoint(sketch, "E560", {"position": v(3.32, -16.67) * mm});
            skPoint(sketch, "E561", {"position": v(3.51, -17.65) * mm});
            skPoint(sketch, "E562", {"position": v(3.7, -18.63) * mm});
            skPoint(sketch, "E563", {"position": v(3.9, -19.62) * mm});
            skPoint(sketch, "E564", {"position": v(4.1, -20.6) * mm});
            skPoint(sketch, "E565", {"position": v(4.3, -21.58) * mm});
            skPoint(sketch, "E566", {"position": v(4.49, -22.56) * mm});
            skPoint(sketch, "E567", {"position": v(4.68, -23.54) * mm});
            skPoint(sketch, "E568", {"position": v(4.88, -24.52) * mm});
            skPoint(sketch, "E569", {"position": v(5.07, -25.5) * mm});
            skPoint(sketch, "E570", {"position": v(5.27, -26.48) * mm});
            skPoint(sketch, "E571", {"position": v(5.46, -27.46) * mm});
            skPoint(sketch, "E572", {"position": v(10.72, -25.87) * mm});
            skPoint(sketch, "E573", {"position": v(10.33, -24.94) * mm});
            skPoint(sketch, "E574", {"position": v(9.95, -24.02) * mm});
            skPoint(sketch, "E575", {"position": v(9.57, -23.1) * mm});
            skPoint(sketch, "E576", {"position": v(9.18, -22.17) * mm});
            skPoint(sketch, "E577", {"position": v(8.8, -21.25) * mm});
            skPoint(sketch, "E578", {"position": v(8.42, -20.33) * mm});
            skPoint(sketch, "E579", {"position": v(8.04, -19.4) * mm});
            skPoint(sketch, "E580", {"position": v(7.65, -18.48) * mm});
            skPoint(sketch, "E581", {"position": v(7.27, -17.55) * mm});
            skPoint(sketch, "E582", {"position": v(6.89, -16.63) * mm});
            skPoint(sketch, "E583", {"position": v(6.5, -15.7) * mm});
            skPoint(sketch, "E584", {"position": v(6.12, -14.78) * mm});
            skPoint(sketch, "E585", {"position": v(5.74, -13.86) * mm});
            skPoint(sketch, "E586", {"position": v(5.36, -12.93) * mm});
            skPoint(sketch, "E587", {"position": v(4.97, -12.01) * mm});
            skPoint(sketch, "E588", {"position": v(7.22, -10.8) * mm});
            skPoint(sketch, "E589", {"position": v(7.78, -11.64) * mm});
            skPoint(sketch, "E590", {"position": v(8.33, -12.47) * mm});
            skPoint(sketch, "E591", {"position": v(8.89, -13.3) * mm});
            skPoint(sketch, "E592", {"position": v(9.44, -14.13) * mm});
            skPoint(sketch, "E593", {"position": v(10, -14.97) * mm});
            skPoint(sketch, "E594", {"position": v(10.56, -15.8) * mm});
            skPoint(sketch, "E595", {"position": v(11.11, -16.63) * mm});
            skPoint(sketch, "E596", {"position": v(11.67, -17.46) * mm});
            skPoint(sketch, "E597", {"position": v(12.22, -18.3) * mm});
            skPoint(sketch, "E598", {"position": v(12.78, -19.12) * mm});
            skPoint(sketch, "E599", {"position": v(13.33, -19.96) * mm});
            skPoint(sketch, "E600", {"position": v(13.89, -20.79) * mm});
            skPoint(sketch, "E601", {"position": v(14.44, -21.62) * mm});
            skPoint(sketch, "E602", {"position": v(15, -22.45) * mm});
            skPoint(sketch, "E603", {"position": v(15.56, -23.28) * mm});
            skPoint(sketch, "E604", {"position": v(16.11, -24.11) * mm});
            skPoint(sketch, "E605", {"position": v(20.5, -20.5) * mm});
            skPoint(sketch, "E606", {"position": v(9.2, -9.2) * mm});
            skPoint(sketch, "E607", {"position": v(9.9, -9.9) * mm});
            skPoint(sketch, "E608", {"position": v(10.6, -10.6) * mm});
            skPoint(sketch, "E609", {"position": v(11.31, -11.31) * mm});
            skPoint(sketch, "E610", {"position": v(12.02, -12.02) * mm});
            skPoint(sketch, "E611", {"position": v(12.73, -12.73) * mm});
            skPoint(sketch, "E612", {"position": v(13.44, -13.44) * mm});
            skPoint(sketch, "E613", {"position": v(14.14, -14.14) * mm});
            skPoint(sketch, "E614", {"position": v(14.85, -14.85) * mm});
            skPoint(sketch, "E615", {"position": v(15.56, -15.56) * mm});
            skPoint(sketch, "E616", {"position": v(16.26, -16.26) * mm});
            skPoint(sketch, "E617", {"position": v(16.97, -16.97) * mm});
            skPoint(sketch, "E618", {"position": v(17.68, -17.68) * mm});
            skPoint(sketch, "E619", {"position": v(18.38, -18.38) * mm});
            skPoint(sketch, "E620", {"position": v(19.1, -19.1) * mm});
            skPoint(sketch, "E621", {"position": v(19.8, -19.8) * mm});
            skPoint(sketch, "E622", {"position": v(24.11, -16.11) * mm});
            skPoint(sketch, "E623", {"position": v(23.28, -15.56) * mm});
            skPoint(sketch, "E624", {"position": v(22.45, -15) * mm});
            skPoint(sketch, "E625", {"position": v(21.62, -14.44) * mm});
            skPoint(sketch, "E626", {"position": v(20.79, -13.89) * mm});
            skPoint(sketch, "E627", {"position": v(19.96, -13.33) * mm});
            skPoint(sketch, "E628", {"position": v(19.12, -12.78) * mm});
            skPoint(sketch, "E629", {"position": v(18.3, -12.22) * mm});
            skPoint(sketch, "E630", {"position": v(17.46, -11.67) * mm});
            skPoint(sketch, "E631", {"position": v(16.63, -11.11) * mm});
            skPoint(sketch, "E632", {"position": v(15.8, -10.56) * mm});
            skPoint(sketch, "E633", {"position": v(14.97, -10) * mm});
            skPoint(sketch, "E634", {"position": v(14.13, -9.44) * mm});
            skPoint(sketch, "E635", {"position": v(13.3, -8.89) * mm});
            skPoint(sketch, "E636", {"position": v(12.47, -8.33) * mm});
            skPoint(sketch, "E637", {"position": v(11.64, -7.78) * mm});
            skPoint(sketch, "E638", {"position": v(10.8, -7.22) * mm});
            skPoint(sketch, "E639", {"position": v(12.01, -4.97) * mm});
            skPoint(sketch, "E640", {"position": v(12.93, -5.36) * mm});
            skPoint(sketch, "E641", {"position": v(13.86, -5.74) * mm});
            skPoint(sketch, "E642", {"position": v(14.78, -6.12) * mm});
            skPoint(sketch, "E643", {"position": v(15.7, -6.5) * mm});
            skPoint(sketch, "E644", {"position": v(16.63, -6.89) * mm});
            skPoint(sketch, "E645", {"position": v(17.55, -7.27) * mm});
            skPoint(sketch, "E646", {"position": v(18.48, -7.65) * mm});
            skPoint(sketch, "E647", {"position": v(19.4, -8.04) * mm});
            skPoint(sketch, "E648", {"position": v(20.33, -8.42) * mm});
            skPoint(sketch, "E649", {"position": v(21.25, -8.8) * mm});
            skPoint(sketch, "E650", {"position": v(22.17, -9.18) * mm});
            skPoint(sketch, "E651", {"position": v(23.1, -9.57) * mm});
            skPoint(sketch, "E652", {"position": v(24.02, -9.95) * mm});
            skPoint(sketch, "E653", {"position": v(24.94, -10.33) * mm});
            skPoint(sketch, "E654", {"position": v(25.87, -10.72) * mm});
            skPoint(sketch, "E655", {"position": v(26.8, -11.1) * mm});
            skPoint(sketch, "E656", {"position": v(12.75, -2.54) * mm});
            skPoint(sketch, "E657", {"position": v(13.73, -2.73) * mm});
            skPoint(sketch, "E658", {"position": v(14.71, -2.93) * mm});
            skPoint(sketch, "E659", {"position": v(15.7, -3.12) * mm});
            skPoint(sketch, "E660", {"position": v(16.67, -3.32) * mm});
            skPoint(sketch, "E661", {"position": v(17.65, -3.51) * mm});
            skPoint(sketch, "E662", {"position": v(18.63, -3.7) * mm});
            skPoint(sketch, "E663", {"position": v(19.62, -3.9) * mm});
            skPoint(sketch, "E664", {"position": v(20.6, -4.1) * mm});
            skPoint(sketch, "E665", {"position": v(21.58, -4.3) * mm});
            skPoint(sketch, "E666", {"position": v(22.56, -4.49) * mm});
            skPoint(sketch, "E667", {"position": v(23.54, -4.68) * mm});
            skPoint(sketch, "E668", {"position": v(24.52, -4.88) * mm});
            skPoint(sketch, "E669", {"position": v(25.5, -5.07) * mm});
            skPoint(sketch, "E670", {"position": v(26.48, -5.27) * mm});
            skPoint(sketch, "E671", {"position": v(27.46, -5.46) * mm});
            skPoint(sketch, "E672", {"position": v(28.44, -5.66) * mm});
            skPoint(sketch, "E673", {"position": v(13, 0) * mm});
            skPoint(sketch, "E674", {"position": v(14, 0) * mm});
            skPoint(sketch, "E675", {"position": v(15, 0) * mm});
            skPoint(sketch, "E676", {"position": v(16, 0) * mm});
            skPoint(sketch, "E677", {"position": v(17, 0) * mm});
            skPoint(sketch, "E678", {"position": v(18, 0) * mm});
            skPoint(sketch, "E679", {"position": v(19, 0) * mm});
            skPoint(sketch, "E680", {"position": v(20, 0) * mm});
            skPoint(sketch, "E681", {"position": v(21, 0) * mm});
            skPoint(sketch, "E682", {"position": v(22, 0) * mm});
            skPoint(sketch, "E683", {"position": v(23, 0) * mm});
            skPoint(sketch, "E684", {"position": v(24, 0) * mm});
            skPoint(sketch, "E685", {"position": v(25, 0) * mm});
            skPoint(sketch, "E686", {"position": v(26, 0) * mm});
            skPoint(sketch, "E687", {"position": v(27, 0) * mm});
            skPoint(sketch, "E688", {"position": v(28, 0) * mm});
            skPoint(sketch, "E689", {"position": v(29, 0) * mm});
            skPoint(sketch, "E690", {"position": v(28.44, 5.66) * mm});
            skPoint(sketch, "E691", {"position": v(27.46, 5.46) * mm});
            skPoint(sketch, "E692", {"position": v(26.48, 5.27) * mm});
            skPoint(sketch, "E693", {"position": v(25.5, 5.07) * mm});
            skPoint(sketch, "E694", {"position": v(24.52, 4.88) * mm});
            skPoint(sketch, "E695", {"position": v(23.54, 4.68) * mm});
            skPoint(sketch, "E696", {"position": v(22.56, 4.49) * mm});
            skPoint(sketch, "E697", {"position": v(21.58, 4.3) * mm});
            skPoint(sketch, "E698", {"position": v(20.6, 4.1) * mm});
            skPoint(sketch, "E699", {"position": v(19.62, 3.9) * mm});
            skPoint(sketch, "E700", {"position": v(18.63, 3.7) * mm});
            skPoint(sketch, "E701", {"position": v(17.65, 3.51) * mm});
            skPoint(sketch, "E702", {"position": v(16.67, 3.32) * mm});
            skPoint(sketch, "E703", {"position": v(15.7, 3.12) * mm});
            skPoint(sketch, "E704", {"position": v(14.71, 2.93) * mm});
            skPoint(sketch, "E705", {"position": v(13.73, 2.73) * mm});
            skPoint(sketch, "E706", {"position": v(12.75, 2.54) * mm});
            skPoint(sketch, "E707", {"position": v(12.01, 4.97) * mm});
            skPoint(sketch, "E708", {"position": v(12.93, 5.36) * mm});
            skPoint(sketch, "E709", {"position": v(13.86, 5.74) * mm});
            skPoint(sketch, "E710", {"position": v(14.78, 6.12) * mm});
            skPoint(sketch, "E711", {"position": v(15.7, 6.5) * mm});
            skPoint(sketch, "E712", {"position": v(16.63, 6.89) * mm});
            skPoint(sketch, "E713", {"position": v(17.55, 7.27) * mm});
            skPoint(sketch, "E714", {"position": v(18.48, 7.65) * mm});
            skPoint(sketch, "E715", {"position": v(19.4, 8.04) * mm});
            skPoint(sketch, "E716", {"position": v(20.33, 8.42) * mm});
            skPoint(sketch, "E717", {"position": v(21.25, 8.8) * mm});
            skPoint(sketch, "E718", {"position": v(22.17, 9.18) * mm});
            skPoint(sketch, "E719", {"position": v(23.1, 9.57) * mm});
            skPoint(sketch, "E720", {"position": v(24.02, 9.95) * mm});
            skPoint(sketch, "E721", {"position": v(24.94, 10.33) * mm});
            skPoint(sketch, "E722", {"position": v(25.87, 10.72) * mm});
            skPoint(sketch, "E723", {"position": v(26.8, 11.1) * mm});
            skPoint(sketch, "E724", {"position": v(9.2, 9.2) * mm});
            skPoint(sketch, "E725", {"position": v(9.9, 9.9) * mm});
            skPoint(sketch, "E726", {"position": v(10.6, 10.6) * mm});
            skPoint(sketch, "E727", {"position": v(11.31, 11.31) * mm});
            skPoint(sketch, "E728", {"position": v(12.02, 12.02) * mm});
            skPoint(sketch, "E729", {"position": v(12.73, 12.73) * mm});
            skPoint(sketch, "E730", {"position": v(13.44, 13.44) * mm});
            skPoint(sketch, "E731", {"position": v(14.14, 14.14) * mm});
            skPoint(sketch, "E732", {"position": v(14.85, 14.85) * mm});
            skPoint(sketch, "E733", {"position": v(15.56, 15.56) * mm});
            skPoint(sketch, "E734", {"position": v(16.26, 16.26) * mm});
            skPoint(sketch, "E735", {"position": v(16.97, 16.97) * mm});
            skPoint(sketch, "E736", {"position": v(17.68, 17.68) * mm});
            skPoint(sketch, "E737", {"position": v(18.38, 18.38) * mm});
            skPoint(sketch, "E738", {"position": v(19.1, 19.1) * mm});
            skPoint(sketch, "E739", {"position": v(19.8, 19.8) * mm});
            skPoint(sketch, "E740", {"position": v(20.5, 20.5) * mm});
            skPoint(sketch, "E741", {"position": v(7.22, 10.8) * mm});
            skPoint(sketch, "E742", {"position": v(7.78, 11.64) * mm});
            skPoint(sketch, "E743", {"position": v(8.33, 12.47) * mm});
            skPoint(sketch, "E744", {"position": v(8.89, 13.3) * mm});
            skPoint(sketch, "E745", {"position": v(9.44, 14.13) * mm});
            skPoint(sketch, "E746", {"position": v(10, 14.97) * mm});
            skPoint(sketch, "E747", {"position": v(10.56, 15.8) * mm});
            skPoint(sketch, "E748", {"position": v(11.11, 16.63) * mm});
            skPoint(sketch, "E749", {"position": v(11.67, 17.46) * mm});
            skPoint(sketch, "E750", {"position": v(12.22, 18.3) * mm});
            skPoint(sketch, "E751", {"position": v(12.78, 19.12) * mm});
            skPoint(sketch, "E752", {"position": v(13.33, 19.96) * mm});
            skPoint(sketch, "E753", {"position": v(13.89, 20.79) * mm});
            skPoint(sketch, "E754", {"position": v(14.44, 21.62) * mm});
            skPoint(sketch, "E755", {"position": v(15, 22.45) * mm});
            skPoint(sketch, "E756", {"position": v(15.56, 23.28) * mm});
            skPoint(sketch, "E757", {"position": v(16.11, 24.11) * mm});
            skPoint(sketch, "E758", {"position": v(-26.8, 11.1) * mm});
            skPoint(sketch, "E759", {"position": v(-25.87, 10.72) * mm});
            skPoint(sketch, "E760", {"position": v(-24.94, 10.33) * mm});
            skPoint(sketch, "E761", {"position": v(-24.02, 9.95) * mm});
            skPoint(sketch, "E762", {"position": v(-23.1, 9.57) * mm});
            skPoint(sketch, "E763", {"position": v(-22.17, 9.18) * mm});
            skPoint(sketch, "E764", {"position": v(-21.25, 8.8) * mm});
            skPoint(sketch, "E765", {"position": v(-20.33, 8.42) * mm});
            skPoint(sketch, "E766", {"position": v(-19.4, 8.04) * mm});
            skPoint(sketch, "E767", {"position": v(-18.48, 7.65) * mm});
            skPoint(sketch, "E768", {"position": v(-17.55, 7.27) * mm});
            skPoint(sketch, "E769", {"position": v(-16.63, 6.89) * mm});
            skPoint(sketch, "E770", {"position": v(-15.7, 6.5) * mm});
            skPoint(sketch, "E771", {"position": v(-14.78, 6.12) * mm});
            skPoint(sketch, "E772", {"position": v(-13.86, 5.74) * mm});
            skPoint(sketch, "E773", {"position": v(-12.93, 5.36) * mm});
            skPoint(sketch, "E774", {"position": v(-12.01, 4.97) * mm});
            skPoint(sketch, "E775", {"position": v(-11.09, 4.6) * mm});
            skPoint(sketch, "E776", {"position": v(10.8, 7.22) * mm});
            skPoint(sketch, "E777", {"position": v(11.64, 7.78) * mm});
            skPoint(sketch, "E778", {"position": v(12.47, 8.33) * mm});
            skPoint(sketch, "E779", {"position": v(13.3, 8.89) * mm});
            skPoint(sketch, "E780", {"position": v(14.13, 9.44) * mm});
            skPoint(sketch, "E781", {"position": v(14.97, 10) * mm});
            skPoint(sketch, "E782", {"position": v(15.8, 10.56) * mm});
            skPoint(sketch, "E783", {"position": v(16.63, 11.11) * mm});
            skPoint(sketch, "E784", {"position": v(17.46, 11.67) * mm});
            skPoint(sketch, "E785", {"position": v(18.3, 12.22) * mm});
            skPoint(sketch, "E786", {"position": v(19.12, 12.78) * mm});
            skPoint(sketch, "E787", {"position": v(19.96, 13.33) * mm});
            skPoint(sketch, "E788", {"position": v(20.79, 13.89) * mm});
            skPoint(sketch, "E789", {"position": v(21.62, 14.44) * mm});
            skPoint(sketch, "E790", {"position": v(22.45, 15) * mm});
            skPoint(sketch, "E791", {"position": v(23.28, 15.56) * mm});
            skPoint(sketch, "E792", {"position": v(24.11, 16.11) * mm});
            skPoint(sketch, "E793", {"position": v(4.97, 12.01) * mm});
            skPoint(sketch, "E794", {"position": v(5.36, 12.93) * mm});
            skPoint(sketch, "E795", {"position": v(0, 19) * mm});
            skPoint(sketch, "E796", {"position": v(0, 20) * mm});
            skPoint(sketch, "E797", {"position": v(0, 21) * mm});
            skPoint(sketch, "E798", {"position": v(0, 22) * mm});
            skPoint(sketch, "E799", {"position": v(0, 23) * mm});
            skPoint(sketch, "E800", {"position": v(5.74, 13.86) * mm});
            skPoint(sketch, "E801", {"position": v(6.12, 14.78) * mm});
            skPoint(sketch, "E802", {"position": v(6.5, 15.7) * mm});
            skPoint(sketch, "E803", {"position": v(6.89, 16.63) * mm});
            skPoint(sketch, "E804", {"position": v(7.27, 17.55) * mm});
            skPoint(sketch, "E805", {"position": v(7.65, 18.48) * mm});
            skPoint(sketch, "E806", {"position": v(8.04, 19.4) * mm});
            skPoint(sketch, "E807", {"position": v(8.42, 20.33) * mm});
            skPoint(sketch, "E808", {"position": v(8.8, 21.25) * mm});
            skPoint(sketch, "E809", {"position": v(9.18, 22.17) * mm});
            skPoint(sketch, "E810", {"position": v(9.57, 23.1) * mm});
            skPoint(sketch, "E811", {"position": v(9.95, 24.02) * mm});
            skPoint(sketch, "E812", {"position": v(10.33, 24.94) * mm});
            skPoint(sketch, "E813", {"position": v(10.72, 25.87) * mm});
            skPoint(sketch, "E814", {"position": v(11.1, 26.8) * mm});
            skPoint(sketch, "E815", {"position": v(2.54, 12.75) * mm});
            skPoint(sketch, "E816", {"position": v(2.73, 13.73) * mm});
            skPoint(sketch, "E817", {"position": v(2.93, 14.71) * mm});
            skPoint(sketch, "E818", {"position": v(3.12, 15.7) * mm});
            skPoint(sketch, "E819", {"position": v(3.32, 16.67) * mm});
            skPoint(sketch, "E820", {"position": v(3.51, 17.65) * mm});
            skPoint(sketch, "E821", {"position": v(3.7, 18.63) * mm});
            skPoint(sketch, "E822", {"position": v(3.9, 19.62) * mm});
            skPoint(sketch, "E823", {"position": v(4.1, 20.6) * mm});
            skPoint(sketch, "E824", {"position": v(4.3, 21.58) * mm});
            skPoint(sketch, "E825", {"position": v(4.49, 22.56) * mm});
            skPoint(sketch, "E826", {"position": v(4.68, 23.54) * mm});
            skPoint(sketch, "E827", {"position": v(4.88, 24.52) * mm});
            skPoint(sketch, "E828", {"position": v(5.07, 25.5) * mm});
            skPoint(sketch, "E829", {"position": v(5.27, 26.48) * mm});
            skPoint(sketch, "E830", {"position": v(5.46, 27.46) * mm});
            skPoint(sketch, "E831", {"position": v(5.66, 28.44) * mm});
            skPoint(sketch, "E832", {"position": v(0, 24) * mm});
            skPoint(sketch, "E833", {"position": v(0, 25) * mm});
            skPoint(sketch, "E834", {"position": v(0, 26) * mm});
            skPoint(sketch, "E835", {"position": v(0, 27) * mm});
            skPoint(sketch, "E836", {"position": v(0, 28) * mm});
            skPoint(sketch, "E837", {"position": v(0, 29) * mm});
            skPoint(sketch, "E838", {"position": v(-5.66, 28.44) * mm});
            skPoint(sketch, "E839", {"position": v(-5.46, 27.46) * mm});
            skPoint(sketch, "E840", {"position": v(-2.34, 11.77) * mm});
            skPoint(sketch, "E841", {"position": v(-4.6, 11.09) * mm});
            skPoint(sketch, "E842", {"position": v(-6.67, 9.98) * mm});
            skPoint(sketch, "E843", {"position": v(-8.49, 8.49) * mm});
            skPoint(sketch, "E844", {"position": v(-9.98, 6.67) * mm});
            skPoint(sketch, "E845", {"position": v(-10.8, 7.22) * mm});
            skPoint(sketch, "E846", {"position": v(-9.2, 9.2) * mm});
            skPoint(sketch, "E847", {"position": v(-7.78, 11.64) * mm});
            skPoint(sketch, "E848", {"position": v(-7.22, 10.8) * mm});
            skPoint(sketch, "E849", {"position": v(-4.97, 12.01) * mm});
            skPoint(sketch, "E850", {"position": v(-2.54, 12.75) * mm});
            skPoint(sketch, "E851", {"position": v(-2.73, 13.73) * mm});
            skPoint(sketch, "E852", {"position": v(-2.93, 14.71) * mm});
            skPoint(sketch, "E853", {"position": v(-3.12, 15.7) * mm});
            skPoint(sketch, "E854", {"position": v(-3.32, 16.67) * mm});
            skPoint(sketch, "E855", {"position": v(-3.51, 17.65) * mm});
            skPoint(sketch, "E856", {"position": v(-3.7, 18.63) * mm});
            skPoint(sketch, "E857", {"position": v(-3.9, 19.62) * mm});
            skPoint(sketch, "E858", {"position": v(-4.1, 20.6) * mm});
            skPoint(sketch, "E859", {"position": v(-4.3, 21.58) * mm});
            skPoint(sketch, "E860", {"position": v(-4.49, 22.56) * mm});
            skPoint(sketch, "E861", {"position": v(-4.68, 23.54) * mm});
            skPoint(sketch, "E862", {"position": v(-4.88, 24.52) * mm});
            skPoint(sketch, "E863", {"position": v(-5.07, 25.5) * mm});
            skPoint(sketch, "E864", {"position": v(-5.27, 26.48) * mm});
            skPoint(sketch, "E865", {"position": v(-5.36, 12.93) * mm});
            skPoint(sketch, "E866", {"position": v(-9.9, 9.9) * mm});
            skPoint(sketch, "E867", {"position": v(-11.64, 7.78) * mm});
            skPoint(sketch, "E868", {"position": v(-12.47, 8.33) * mm});
            skPoint(sketch, "E869", {"position": v(-10.6, 10.6) * mm});
            skPoint(sketch, "E870", {"position": v(-8.33, 12.47) * mm});
            skPoint(sketch, "E871", {"position": v(-5.74, 13.86) * mm});
            skPoint(sketch, "E872", {"position": v(-6.12, 14.78) * mm});
            skPoint(sketch, "E873", {"position": v(-8.89, 13.3) * mm});
            skPoint(sketch, "E874", {"position": v(-11.31, 11.31) * mm});
            skPoint(sketch, "E875", {"position": v(-13.3, 8.89) * mm});
            skPoint(sketch, "E876", {"position": v(-6.5, 15.7) * mm});
            skPoint(sketch, "E877", {"position": v(-6.89, 16.63) * mm});
            skPoint(sketch, "E878", {"position": v(-7.27, 17.55) * mm});
            skPoint(sketch, "E879", {"position": v(-7.65, 18.48) * mm});
            skPoint(sketch, "E880", {"position": v(-8.04, 19.4) * mm});
            skPoint(sketch, "E881", {"position": v(-8.42, 20.33) * mm});
            skPoint(sketch, "E882", {"position": v(-8.8, 21.25) * mm});
            skPoint(sketch, "E883", {"position": v(-9.18, 22.17) * mm});
            skPoint(sketch, "E884", {"position": v(-9.57, 23.1) * mm});
            skPoint(sketch, "E885", {"position": v(-9.95, 24.02) * mm});
            skPoint(sketch, "E886", {"position": v(-10.33, 24.94) * mm});
            skPoint(sketch, "E887", {"position": v(-10.72, 25.87) * mm});
            skPoint(sketch, "E888", {"position": v(-11.1, 26.8) * mm});
            skPoint(sketch, "E889", {"position": v(-9.44, 14.13) * mm});
            skPoint(sketch, "E890", {"position": v(-12.02, 12.02) * mm});
            skPoint(sketch, "E891", {"position": v(-14.13, 9.44) * mm});
            skPoint(sketch, "E892", {"position": v(-14.97, 10) * mm});
            skPoint(sketch, "E893", {"position": v(-12.73, 12.73) * mm});
            skPoint(sketch, "E894", {"position": v(-10, 14.97) * mm});
            skPoint(sketch, "E895", {"position": v(-10.56, 15.8) * mm});
            skPoint(sketch, "E896", {"position": v(-14.14, 14.14) * mm});
            skPoint(sketch, "E897", {"position": v(-16.63, 11.11) * mm});
            skPoint(sketch, "E898", {"position": v(-11.67, 17.46) * mm});
            skPoint(sketch, "E899", {"position": v(-11.1, 16.6) * mm});
            skPoint(sketch, "E900", {"position": v(-14.85, 14.85) * mm});
            skPoint(sketch, "E901", {"position": v(-17.46, 11.67) * mm});
            skPoint(sketch, "E902", {"position": v(-18.3, 12.22) * mm});
            skPoint(sketch, "E903", {"position": v(-15.56, 15.56) * mm});
            skPoint(sketch, "E904", {"position": v(-12.22, 18.3) * mm});
            skPoint(sketch, "E905", {"position": v(-12.78, 19.12) * mm});
            skPoint(sketch, "E906", {"position": v(-16.26, 16.26) * mm});
            skPoint(sketch, "E907", {"position": v(-19.12, 12.78) * mm});
            skPoint(sketch, "E908", {"position": v(-19.96, 13.33) * mm});
            skPoint(sketch, "E909", {"position": v(-16.97, 16.97) * mm});
            skPoint(sketch, "E910", {"position": v(-13.33, 19.96) * mm});
            skPoint(sketch, "E911", {"position": v(-13.89, 20.79) * mm});
            skPoint(sketch, "E912", {"position": v(-17.68, 17.68) * mm});
            skPoint(sketch, "E913", {"position": v(-20.79, 13.89) * mm});
            skPoint(sketch, "E914", {"position": v(-21.62, 14.44) * mm});
            skPoint(sketch, "E915", {"position": v(-18.38, 18.38) * mm});
            skPoint(sketch, "E916", {"position": v(-14.44, 21.62) * mm});
            skPoint(sketch, "E917", {"position": v(-15, 22.45) * mm});
            skPoint(sketch, "E918", {"position": v(-15.56, 23.28) * mm});
            skPoint(sketch, "E919", {"position": v(-16.11, 24.11) * mm});
            skPoint(sketch, "E920", {"position": v(-19.1, 19.1) * mm});
            skPoint(sketch, "E921", {"position": v(-19.8, 19.8) * mm});
            skPoint(sketch, "E922", {"position": v(-20.5, 20.5) * mm});
            skPoint(sketch, "E923", {"position": v(-15.8, 10.56) * mm});
            skPoint(sketch, "E924", {"position": v(-22.45, 15) * mm});
            skPoint(sketch, "E925", {"position": v(-23.28, 15.56) * mm});
            skPoint(sketch, "E926", {"position": v(-24.11, 16.11) * mm});
            skPoint(sketch, "E927", {"position": v(-0.4, 1.96) * mm});
            skPoint(sketch, "E928", {"position": v(-0.77, 1.85) * mm});
            skPoint(sketch, "E929", {"position": v(-1.11, 1.66) * mm});
            skPoint(sketch, "E930", {"position": v(-1.41, 1.41) * mm});
            skPoint(sketch, "E931", {"position": v(-1.66, 1.11) * mm});
            skPoint(sketch, "E932", {"position": v(-1.85, 0.77) * mm});
            skPoint(sketch, "E933", {"position": v(-1.96, 0.4) * mm});
            skPoint(sketch, "E934", {"position": v(-2, 0) * mm});
            skPoint(sketch, "E935", {"position": v(-1.96, -0.4) * mm});
            skPoint(sketch, "E936", {"position": v(-1.85, -0.77) * mm});
            skPoint(sketch, "E937", {"position": v(-1.66, -1.11) * mm});
            skPoint(sketch, "E938", {"position": v(-1.41, -1.41) * mm});
            skPoint(sketch, "E939", {"position": v(-1.11, -1.66) * mm});
            skPoint(sketch, "E940", {"position": v(-0.77, -1.85) * mm});
            skPoint(sketch, "E941", {"position": v(-0.4, -1.96) * mm});
            skPoint(sketch, "E942", {"position": v(0.4, -1.96) * mm});
            skPoint(sketch, "E943", {"position": v(0.77, -1.85) * mm});
            skPoint(sketch, "E944", {"position": v(1.11, -1.66) * mm});
            skPoint(sketch, "E945", {"position": v(1.41, -1.41) * mm});
            skPoint(sketch, "E946", {"position": v(1.66, -1.11) * mm});
            skPoint(sketch, "E947", {"position": v(1.85, -0.77) * mm});
            skPoint(sketch, "E948", {"position": v(1.96, -0.4) * mm});
            skPoint(sketch, "E949", {"position": v(2, 0) * mm});
            skPoint(sketch, "E950", {"position": v(1.96, 0.4) * mm});
            skPoint(sketch, "E951", {"position": v(1.85, 0.77) * mm});
            skPoint(sketch, "E952", {"position": v(1.66, 1.11) * mm});
            skPoint(sketch, "E953", {"position": v(1.41, 1.41) * mm});
            skPoint(sketch, "E954", {"position": v(1.11, 1.66) * mm});
            skPoint(sketch, "E955", {"position": v(0.77, 1.85) * mm});
            skPoint(sketch, "E956", {"position": v(0.4, 1.96) * mm});
            skPoint(sketch, "E957", {"position": v(-13.44, 13.44) * mm});
            skSolve(sketch);
        }
        {
            var Q0;
            Q0=makeQuery(id+"F1.opRevolve","SWEPT_EDGE",EDGE,{"disambiguationData":[OSD([sQuery(id+"F0.wireOp",EDGE,"E1"),sQuery(id+"F0.wireOp",EDGE,"E2")])]});
            var Q1;
            Q1=makeQuery(id+"F1.opRevolve","SWEPT_FACE",FACE,{"disambiguationData":[OSD([sQuery(id+"F0.wireOp",EDGE,"E1")])]});
            fillet(context, id + "F3", {"entities" : qUnion([Q0, Q1]), "radius" : 0.9 * mm, "tangentPropagation" : true, "allowEdgeOverflow" : false});
        }
        {
            var Q0;
            Q0=sQuery(id+"F2.wireOp",VERTEX,"E5.center");
            var Q1;
            Q1=sQuery(id+"F2.wireOp",VERTEX,"E934");
            var Q2;
            Q2=sQuery(id+"F2.wireOp",VERTEX,"E930");
            var Q3;
            Q3=sQuery(id+"F2.wireOp",VERTEX,"E69");
            var Q4;
            Q4=sQuery(id+"F2.wireOp",VERTEX,"E953");
            var Q5;
            Q5=sQuery(id+"F2.wireOp",VERTEX,"E949");
            var Q6;
            Q6=sQuery(id+"F2.wireOp",VERTEX,"E945");
            var Q7;
            Q7=sQuery(id+"F2.wireOp",VERTEX,"E63");
            var Q8;
            Q8=sQuery(id+"F2.wireOp",VERTEX,"E938");
            var Q9;
            Q9=makeQuery(id+"F1.opRevolve","SWEPT_BODY",BODY,{"disambiguationData":[OSD([sQuery(id+"F0.wireOp",EDGE,"E0"),sQuery(id+"F0.wireOp",EDGE,"E1"),sQuery(id+"F0.wireOp",EDGE,"E2"),sQuery(id+"F0.wireOp",EDGE,"E3")])]});
            hole(context, id + "F4", {"style" : HoleStyle.SIMPLE, "endStyle" : HoleEndStyle.BLIND, "holeDiameter" : 1.2 * mm, "holeDepth" : 2 * mm, "tappedDepth" : 12 * mm, "tapClearance" : 3, "locations" : qUnion([Q0, Q1, Q2, Q3, Q4, Q5, Q6, Q7, Q8]), "scope" : qUnion([Q9])});
        }
        {
            var Q0;
            Q0=sQuery(id+"F2.wireOp",VERTEX,"E131");
            var Q1;
            Q1=sQuery(id+"F2.wireOp",VERTEX,"E104");
            var Q2;
            Q2=sQuery(id+"F2.wireOp",VERTEX,"E108");
            var Q3;
            Q3=sQuery(id+"F2.wireOp",VERTEX,"E112");
            var Q4;
            Q4=sQuery(id+"F2.wireOp",VERTEX,"E116");
            var Q5;
            Q5=sQuery(id+"F2.wireOp",VERTEX,"E119");
            var Q6;
            Q6=sQuery(id+"F2.wireOp",VERTEX,"E123");
            var Q7;
            Q7=sQuery(id+"F2.wireOp",VERTEX,"E127");
            var Q8;
            Q8=sQuery(id+"F2.wireOp",VERTEX,"E160");
            var Q9;
            Q9=sQuery(id+"F2.wireOp",VERTEX,"E133");
            var Q10;
            Q10=sQuery(id+"F2.wireOp",VERTEX,"E137");
            var Q11;
            Q11=sQuery(id+"F2.wireOp",VERTEX,"E141");
            var Q12;
            Q12=sQuery(id+"F2.wireOp",VERTEX,"E145");
            var Q13;
            Q13=sQuery(id+"F2.wireOp",VERTEX,"E66");
            var Q14;
            Q14=sQuery(id+"F2.wireOp",VERTEX,"E152");
            var Q15;
            Q15=sQuery(id+"F2.wireOp",VERTEX,"E156");
            var Q16;
            Q16=makeQuery(id+"F1.opRevolve","SWEPT_BODY",BODY,{"disambiguationData":[OSD([sQuery(id+"F0.wireOp",EDGE,"E0"),sQuery(id+"F0.wireOp",EDGE,"E1"),sQuery(id+"F0.wireOp",EDGE,"E2"),sQuery(id+"F0.wireOp",EDGE,"E3")])]});
            hole(context, id + "F5", {"style" : HoleStyle.SIMPLE, "endStyle" : HoleEndStyle.BLIND, "holeDiameter" : 1.2 * mm, "holeDepth" : 2 * mm, "tappedDepth" : 12 * mm, "tapClearance" : 3, "locations" : qUnion([Q0, Q1, Q2, Q3, Q4, Q5, Q6, Q7, Q8, Q9, Q10, Q11, Q12, Q13, Q14, Q15]), "scope" : qUnion([Q16])});
        }
        {
            var Q0;
            Q0=sQuery(id+"F2.wireOp",VERTEX,"E177");
            var Q1;
            Q1=sQuery(id+"F2.wireOp",VERTEX,"E181");
            var Q2;
            Q2=sQuery(id+"F2.wireOp",VERTEX,"E185");
            var Q3;
            Q3=sQuery(id+"F2.wireOp",VERTEX,"E189");
            var Q4;
            Q4=sQuery(id+"F2.wireOp",VERTEX,"E192");
            var Q5;
            Q5=sQuery(id+"F2.wireOp",VERTEX,"E196");
            var Q6;
            Q6=sQuery(id+"F2.wireOp",VERTEX,"E200");
            var Q7;
            Q7=sQuery(id+"F2.wireOp",VERTEX,"E204");
            var Q8;
            Q8=sQuery(id+"F2.wireOp",VERTEX,"E243");
            var Q9;
            Q9=sQuery(id+"F2.wireOp",VERTEX,"E245");
            var Q10;
            Q10=sQuery(id+"F2.wireOp",VERTEX,"E247");
            var Q11;
            Q11=sQuery(id+"F2.wireOp",VERTEX,"E249");
            var Q12;
            Q12=sQuery(id+"F2.wireOp",VERTEX,"E251");
            var Q13;
            Q13=sQuery(id+"F2.wireOp",VERTEX,"E253");
            var Q14;
            Q14=sQuery(id+"F2.wireOp",VERTEX,"E255");
            var Q15;
            Q15=sQuery(id+"F2.wireOp",VERTEX,"E257");
            var Q16;
            Q16=sQuery(id+"F2.wireOp",VERTEX,"E259");
            var Q17;
            Q17=sQuery(id+"F2.wireOp",VERTEX,"E261");
            var Q18;
            Q18=sQuery(id+"F2.wireOp",VERTEX,"E263");
            var Q19;
            Q19=sQuery(id+"F2.wireOp",VERTEX,"E265");
            var Q20;
            Q20=sQuery(id+"F2.wireOp",VERTEX,"E236");
            var Q21;
            Q21=sQuery(id+"F2.wireOp",VERTEX,"E237");
            var Q22;
            Q22=sQuery(id+"F2.wireOp",VERTEX,"E239");
            var Q23;
            Q23=sQuery(id+"F2.wireOp",VERTEX,"E241");
            var Q24;
            Q24=makeQuery(id+"F1.opRevolve","SWEPT_BODY",BODY,{"disambiguationData":[OSD([sQuery(id+"F0.wireOp",EDGE,"E0"),sQuery(id+"F0.wireOp",EDGE,"E1"),sQuery(id+"F0.wireOp",EDGE,"E2"),sQuery(id+"F0.wireOp",EDGE,"E3")])]});
            hole(context, id + "F6", {"style" : HoleStyle.SIMPLE, "endStyle" : HoleEndStyle.BLIND, "holeDiameter" : 1.2 * mm, "holeDepth" : 2 * mm, "tappedDepth" : 12 * mm, "tapClearance" : 3, "locations" : qUnion([Q0, Q1, Q2, Q3, Q4, Q5, Q6, Q7, Q8, Q9, Q10, Q11, Q12, Q13, Q14, Q15, Q16, Q17, Q18, Q19, Q20, Q21, Q22, Q23]), "scope" : qUnion([Q24])});
        }
        {
            var Q0;
            Q0=sQuery(id+"F2.wireOp",VERTEX,"E297");
            var Q1;
            Q1=sQuery(id+"F2.wireOp",VERTEX,"E166");
            var Q2;
            Q2=sQuery(id+"F2.wireOp",VERTEX,"E269");
            var Q3;
            Q3=sQuery(id+"F2.wireOp",VERTEX,"E271");
            var Q4;
            Q4=sQuery(id+"F2.wireOp",VERTEX,"E273");
            var Q5;
            Q5=sQuery(id+"F2.wireOp",VERTEX,"E275");
            var Q6;
            Q6=sQuery(id+"F2.wireOp",VERTEX,"E277");
            var Q7;
            Q7=sQuery(id+"F2.wireOp",VERTEX,"E279");
            var Q8;
            Q8=sQuery(id+"F2.wireOp",VERTEX,"E281");
            var Q9;
            Q9=sQuery(id+"F2.wireOp",VERTEX,"E283");
            var Q10;
            Q10=sQuery(id+"F2.wireOp",VERTEX,"E285");
            var Q11;
            Q11=sQuery(id+"F2.wireOp",VERTEX,"E287");
            var Q12;
            Q12=sQuery(id+"F2.wireOp",VERTEX,"E289");
            var Q13;
            Q13=sQuery(id+"F2.wireOp",VERTEX,"E291");
            var Q14;
            Q14=sQuery(id+"F2.wireOp",VERTEX,"E293");
            var Q15;
            Q15=sQuery(id+"F2.wireOp",VERTEX,"E295");
            var Q16;
            Q16=makeQuery(id+"F1.opRevolve","SWEPT_BODY",BODY,{"disambiguationData":[OSD([sQuery(id+"F0.wireOp",EDGE,"E0"),sQuery(id+"F0.wireOp",EDGE,"E1"),sQuery(id+"F0.wireOp",EDGE,"E2"),sQuery(id+"F0.wireOp",EDGE,"E3")])]});
            hole(context, id + "F7", {"style" : HoleStyle.SIMPLE, "endStyle" : HoleEndStyle.BLIND, "holeDiameter" : 1.2 * mm, "holeDepth" : 2 * mm, "tappedDepth" : 12 * mm, "tapClearance" : 3, "locations" : qUnion([Q0, Q1, Q2, Q3, Q4, Q5, Q6, Q7, Q8, Q9, Q10, Q11, Q12, Q13, Q14, Q15]), "scope" : qUnion([Q16])});
        }
        {
            var Q0;
            Q0=sQuery(id+"F2.wireOp",VERTEX,"E329");
            var Q1;
            Q1=sQuery(id+"F2.wireOp",VERTEX,"E330");
            var Q2;
            Q2=sQuery(id+"F2.wireOp",VERTEX,"E332");
            var Q3;
            Q3=sQuery(id+"F2.wireOp",VERTEX,"E334");
            var Q4;
            Q4=sQuery(id+"F2.wireOp",VERTEX,"E336");
            var Q5;
            Q5=sQuery(id+"F2.wireOp",VERTEX,"E338");
            var Q6;
            Q6=sQuery(id+"F2.wireOp",VERTEX,"E340");
            var Q7;
            Q7=sQuery(id+"F2.wireOp",VERTEX,"E342");
            var Q8;
            Q8=sQuery(id+"F2.wireOp",VERTEX,"E344");
            var Q9;
            Q9=sQuery(id+"F2.wireOp",VERTEX,"E346");
            var Q10;
            Q10=sQuery(id+"F2.wireOp",VERTEX,"E348");
            var Q11;
            Q11=sQuery(id+"F2.wireOp",VERTEX,"E350");
            var Q12;
            Q12=sQuery(id+"F2.wireOp",VERTEX,"E352");
            var Q13;
            Q13=sQuery(id+"F2.wireOp",VERTEX,"E354");
            var Q14;
            Q14=sQuery(id+"F2.wireOp",VERTEX,"E356");
            var Q15;
            Q15=sQuery(id+"F2.wireOp",VERTEX,"E358");
            var Q16;
            Q16=makeQuery(id+"F1.opRevolve","SWEPT_BODY",BODY,{"disambiguationData":[OSD([sQuery(id+"F0.wireOp",EDGE,"E0"),sQuery(id+"F0.wireOp",EDGE,"E1"),sQuery(id+"F0.wireOp",EDGE,"E2"),sQuery(id+"F0.wireOp",EDGE,"E3")])]});
            hole(context, id + "F12", {"style" : HoleStyle.SIMPLE, "endStyle" : HoleEndStyle.THROUGH, "holeDiameter" : 1.2 * mm, "tappedDepth" : 12 * mm, "tapClearance" : 3, "locations" : qUnion([Q0, Q1, Q2, Q3, Q4, Q5, Q6, Q7, Q8, Q9, Q10, Q11, Q12, Q13, Q14, Q15]), "scope" : qUnion([Q16])});
        }
        {
            var Q0;
            Q0=sQuery(id+"F2.wireOp",VERTEX,"E170");
            var Q1;
            Q1=sQuery(id+"F2.wireOp",VERTEX,"E849");
            var Q2;
            Q2=sQuery(id+"F2.wireOp",VERTEX,"E793");
            var Q3;
            Q3=sQuery(id+"F2.wireOp",VERTEX,"E724");
            var Q4;
            Q4=sQuery(id+"F2.wireOp",VERTEX,"E707");
            var Q5;
            Q5=sQuery(id+"F2.wireOp",VERTEX,"E673");
            var Q6;
            Q6=sQuery(id+"F2.wireOp",VERTEX,"E639");
            var Q7;
            Q7=sQuery(id+"F2.wireOp",VERTEX,"E606");
            var Q8;
            Q8=sQuery(id+"F2.wireOp",VERTEX,"E587");
            var Q9;
            Q9=sQuery(id+"F2.wireOp",VERTEX,"E540");
            var Q10;
            Q10=sQuery(id+"F2.wireOp",VERTEX,"E523");
            var Q11;
            Q11=sQuery(id+"F2.wireOp",VERTEX,"E470");
            var Q12;
            Q12=sQuery(id+"F2.wireOp",VERTEX,"E436");
            var Q13;
            Q13=sQuery(id+"F2.wireOp",VERTEX,"E400");
            var Q14;
            Q14=sQuery(id+"F2.wireOp",VERTEX,"E774");
            var Q15;
            Q15=sQuery(id+"F2.wireOp",VERTEX,"E846");
            var Q16;
            Q16=makeQuery(id+"F1.opRevolve","SWEPT_BODY",BODY,{"disambiguationData":[OSD([sQuery(id+"F0.wireOp",EDGE,"E0"),sQuery(id+"F0.wireOp",EDGE,"E1"),sQuery(id+"F0.wireOp",EDGE,"E2"),sQuery(id+"F0.wireOp",EDGE,"E3")])]});
            hole(context, id + "F13", {"style" : HoleStyle.SIMPLE, "endStyle" : HoleEndStyle.THROUGH, "holeDiameter" : 1.2 * mm, "tappedDepth" : 12 * mm, "tapClearance" : 3, "locations" : qUnion([Q0, Q1, Q2, Q3, Q4, Q5, Q6, Q7, Q8, Q9, Q10, Q11, Q12, Q13, Q14, Q15]), "scope" : qUnion([Q16])});
        }
        {
            var Q0;
            Q0=sQuery(id+"F2.wireOp",VERTEX,"E847");
            var Q1;
            Q1=sQuery(id+"F2.wireOp",VERTEX,"E851");
            var Q2;
            Q2=sQuery(id+"F2.wireOp",VERTEX,"E816");
            var Q3;
            Q3=sQuery(id+"F2.wireOp",VERTEX,"E742");
            var Q4;
            Q4=sQuery(id+"F2.wireOp",VERTEX,"E777");
            var Q5;
            Q5=sQuery(id+"F2.wireOp",VERTEX,"E705");
            var Q6;
            Q6=sQuery(id+"F2.wireOp",VERTEX,"E657");
            var Q7;
            Q7=sQuery(id+"F2.wireOp",VERTEX,"E637");
            var Q8;
            Q8=sQuery(id+"F2.wireOp",VERTEX,"E589");
            var Q9;
            Q9=sQuery(id+"F2.wireOp",VERTEX,"E557");
            var Q10;
            Q10=sQuery(id+"F2.wireOp",VERTEX,"E525");
            var Q11;
            Q11=sQuery(id+"F2.wireOp",VERTEX,"E488");
            var Q12;
            Q12=sQuery(id+"F2.wireOp",VERTEX,"E454");
            var Q13;
            Q13=sQuery(id+"F2.wireOp",VERTEX,"E434");
            var Q14;
            Q14=sQuery(id+"F2.wireOp",VERTEX,"E416");
            var Q15;
            Q15=sQuery(id+"F2.wireOp",VERTEX,"E867");
            var Q16;
            Q16=makeQuery(id+"F1.opRevolve","SWEPT_BODY",BODY,{"disambiguationData":[OSD([sQuery(id+"F0.wireOp",EDGE,"E0"),sQuery(id+"F0.wireOp",EDGE,"E1"),sQuery(id+"F0.wireOp",EDGE,"E2"),sQuery(id+"F0.wireOp",EDGE,"E3")])]});
            hole(context, id + "F14", {"style" : HoleStyle.SIMPLE, "endStyle" : HoleEndStyle.THROUGH, "holeDiameter" : 1.2 * mm, "tappedDepth" : 12 * mm, "tapClearance" : 3, "locations" : qUnion([Q0, Q1, Q2, Q3, Q4, Q5, Q6, Q7, Q8, Q9, Q10, Q11, Q12, Q13, Q14, Q15]), "scope" : qUnion([Q16])});
        }
        {
            var Q0;
            Q0=sQuery(id+"F2.wireOp",VERTEX,"E173");
            var Q1;
            Q1=sQuery(id+"F2.wireOp",VERTEX,"E801");
            var Q2;
            Q2=sQuery(id+"F2.wireOp",VERTEX,"E727");
            var Q3;
            Q3=sQuery(id+"F2.wireOp",VERTEX,"E710");
            var Q4;
            Q4=sQuery(id+"F2.wireOp",VERTEX,"E676");
            var Q5;
            Q5=sQuery(id+"F2.wireOp",VERTEX,"E642");
            var Q6;
            Q6=sQuery(id+"F2.wireOp",VERTEX,"E609");
            var Q7;
            Q7=sQuery(id+"F2.wireOp",VERTEX,"E584");
            var Q8;
            Q8=sQuery(id+"F2.wireOp",VERTEX,"E543");
            var Q9;
            Q9=sQuery(id+"F2.wireOp",VERTEX,"E520");
            var Q10;
            Q10=sQuery(id+"F2.wireOp",VERTEX,"E473");
            var Q11;
            Q11=sQuery(id+"F2.wireOp",VERTEX,"E439");
            var Q12;
            Q12=sQuery(id+"F2.wireOp",VERTEX,"E397");
            var Q13;
            Q13=sQuery(id+"F2.wireOp",VERTEX,"E771");
            var Q14;
            Q14=sQuery(id+"F2.wireOp",VERTEX,"E874");
            var Q15;
            Q15=sQuery(id+"F2.wireOp",VERTEX,"E872");
            var Q16;
            Q16=makeQuery(id+"F1.opRevolve","SWEPT_BODY",BODY,{"disambiguationData":[OSD([sQuery(id+"F0.wireOp",EDGE,"E0"),sQuery(id+"F0.wireOp",EDGE,"E1"),sQuery(id+"F0.wireOp",EDGE,"E2"),sQuery(id+"F0.wireOp",EDGE,"E3")])]});
            hole(context, id + "F15", {"style" : HoleStyle.SIMPLE, "endStyle" : HoleEndStyle.THROUGH, "holeDiameter" : 1.2 * mm, "tappedDepth" : 12 * mm, "tapClearance" : 3, "locations" : qUnion([Q0, Q1, Q2, Q3, Q4, Q5, Q6, Q7, Q8, Q9, Q10, Q11, Q12, Q13, Q14, Q15]), "scope" : qUnion([Q16])});
        }
        {
            var Q0;
            Q0=sQuery(id+"F2.wireOp",VERTEX,"E854");
            var Q1;
            Q1=sQuery(id+"F2.wireOp",VERTEX,"E819");
            var Q2;
            Q2=sQuery(id+"F2.wireOp",VERTEX,"E745");
            var Q3;
            Q3=sQuery(id+"F2.wireOp",VERTEX,"E780");
            var Q4;
            Q4=sQuery(id+"F2.wireOp",VERTEX,"E702");
            var Q5;
            Q5=sQuery(id+"F2.wireOp",VERTEX,"E660");
            var Q6;
            Q6=sQuery(id+"F2.wireOp",VERTEX,"E634");
            var Q7;
            Q7=sQuery(id+"F2.wireOp",VERTEX,"E592");
            var Q8;
            Q8=sQuery(id+"F2.wireOp",VERTEX,"E560");
            var Q9;
            Q9=sQuery(id+"F2.wireOp",VERTEX,"E528");
            var Q10;
            Q10=sQuery(id+"F2.wireOp",VERTEX,"E491");
            var Q11;
            Q11=sQuery(id+"F2.wireOp",VERTEX,"E457");
            var Q12;
            Q12=sQuery(id+"F2.wireOp",VERTEX,"E431");
            var Q13;
            Q13=sQuery(id+"F2.wireOp",VERTEX,"E413");
            var Q14;
            Q14=sQuery(id+"F2.wireOp",VERTEX,"E891");
            var Q15;
            Q15=sQuery(id+"F2.wireOp",VERTEX,"E889");
            var Q16;
            Q16=makeQuery(id+"F1.opRevolve","SWEPT_BODY",BODY,{"disambiguationData":[OSD([sQuery(id+"F0.wireOp",EDGE,"E0"),sQuery(id+"F0.wireOp",EDGE,"E1"),sQuery(id+"F0.wireOp",EDGE,"E2"),sQuery(id+"F0.wireOp",EDGE,"E3")])]});
            hole(context, id + "F8", {"style" : HoleStyle.SIMPLE, "endStyle" : HoleEndStyle.THROUGH, "holeDiameter" : 1.2 * mm, "tappedDepth" : 12 * mm, "tapClearance" : 3, "locations" : qUnion([Q0, Q1, Q2, Q3, Q4, Q5, Q6, Q7, Q8, Q9, Q10, Q11, Q12, Q13, Q14, Q15]), "scope" : qUnion([Q16])});
        }
        {
            var Q0;
            Q0=sQuery(id+"F2.wireOp",VERTEX,"E795");
            var Q1;
            Q1=sQuery(id+"F2.wireOp",VERTEX,"E804");
            var Q2;
            Q2=sQuery(id+"F2.wireOp",VERTEX,"E730");
            var Q3;
            Q3=sQuery(id+"F2.wireOp",VERTEX,"E713");
            var Q4;
            Q4=sQuery(id+"F2.wireOp",VERTEX,"E679");
            var Q5;
            Q5=sQuery(id+"F2.wireOp",VERTEX,"E645");
            var Q6;
            Q6=sQuery(id+"F2.wireOp",VERTEX,"E612");
            var Q7;
            Q7=sQuery(id+"F2.wireOp",VERTEX,"E581");
            var Q8;
            Q8=sQuery(id+"F2.wireOp",VERTEX,"E546");
            var Q9;
            Q9=sQuery(id+"F2.wireOp",VERTEX,"E517");
            var Q10;
            Q10=sQuery(id+"F2.wireOp",VERTEX,"E476");
            var Q11;
            Q11=sQuery(id+"F2.wireOp",VERTEX,"E442");
            var Q12;
            Q12=sQuery(id+"F2.wireOp",VERTEX,"E394");
            var Q13;
            Q13=sQuery(id+"F2.wireOp",VERTEX,"E768");
            var Q14;
            Q14=sQuery(id+"F2.wireOp",VERTEX,"E878");
            var Q15;
            Q15=sQuery(id+"F2.wireOp",VERTEX,"E957");
            var Q16;
            Q16=makeQuery(id+"F1.opRevolve","SWEPT_BODY",BODY,{"disambiguationData":[OSD([sQuery(id+"F0.wireOp",EDGE,"E0"),sQuery(id+"F0.wireOp",EDGE,"E1"),sQuery(id+"F0.wireOp",EDGE,"E2"),sQuery(id+"F0.wireOp",EDGE,"E3")])]});
            hole(context, id + "F16", {"style" : HoleStyle.SIMPLE, "endStyle" : HoleEndStyle.THROUGH, "holeDiameter" : 1.2 * mm, "tappedDepth" : 12 * mm, "tapClearance" : 3, "locations" : qUnion([Q0, Q1, Q2, Q3, Q4, Q5, Q6, Q7, Q8, Q9, Q10, Q11, Q12, Q13, Q14, Q15]), "scope" : qUnion([Q16])});
        }
        {
            var Q0;
            Q0=sQuery(id+"F2.wireOp",VERTEX,"E857");
            var Q1;
            Q1=sQuery(id+"F2.wireOp",VERTEX,"E822");
            var Q2;
            Q2=sQuery(id+"F2.wireOp",VERTEX,"E748");
            var Q3;
            Q3=sQuery(id+"F2.wireOp",VERTEX,"E783");
            var Q4;
            Q4=sQuery(id+"F2.wireOp",VERTEX,"E699");
            var Q5;
            Q5=sQuery(id+"F2.wireOp",VERTEX,"E663");
            var Q6;
            Q6=sQuery(id+"F2.wireOp",VERTEX,"E631");
            var Q7;
            Q7=sQuery(id+"F2.wireOp",VERTEX,"E595");
            var Q8;
            Q8=sQuery(id+"F2.wireOp",VERTEX,"E563");
            var Q9;
            Q9=sQuery(id+"F2.wireOp",VERTEX,"E531");
            var Q10;
            Q10=sQuery(id+"F2.wireOp",VERTEX,"E494");
            var Q11;
            Q11=sQuery(id+"F2.wireOp",VERTEX,"E460");
            var Q12;
            Q12=sQuery(id+"F2.wireOp",VERTEX,"E428");
            var Q13;
            Q13=sQuery(id+"F2.wireOp",VERTEX,"E410");
            var Q14;
            Q14=sQuery(id+"F2.wireOp",VERTEX,"E897");
            var Q15;
            Q15=sQuery(id+"F2.wireOp",VERTEX,"E899");
            var Q16;
            Q16=makeQuery(id+"F1.opRevolve","SWEPT_BODY",BODY,{"disambiguationData":[OSD([sQuery(id+"F0.wireOp",EDGE,"E0"),sQuery(id+"F0.wireOp",EDGE,"E1"),sQuery(id+"F0.wireOp",EDGE,"E2"),sQuery(id+"F0.wireOp",EDGE,"E3")])]});
            hole(context, id + "F17", {"style" : HoleStyle.SIMPLE, "endStyle" : HoleEndStyle.THROUGH, "holeDiameter" : 1.2 * mm, "tappedDepth" : 12 * mm, "tapClearance" : 3, "locations" : qUnion([Q0, Q1, Q2, Q3, Q4, Q5, Q6, Q7, Q8, Q9, Q10, Q11, Q12, Q13, Q14, Q15]), "scope" : qUnion([Q16])});
        }
        {
            var Q0;
            Q0=sQuery(id+"F2.wireOp",VERTEX,"E798");
            var Q1;
            Q1=sQuery(id+"F2.wireOp",VERTEX,"E807");
            var Q2;
            Q2=sQuery(id+"F2.wireOp",VERTEX,"E733");
            var Q3;
            Q3=sQuery(id+"F2.wireOp",VERTEX,"E716");
            var Q4;
            Q4=sQuery(id+"F2.wireOp",VERTEX,"E682");
            var Q5;
            Q5=sQuery(id+"F2.wireOp",VERTEX,"E648");
            var Q6;
            Q6=sQuery(id+"F2.wireOp",VERTEX,"E615");
            var Q7;
            Q7=sQuery(id+"F2.wireOp",VERTEX,"E578");
            var Q8;
            Q8=sQuery(id+"F2.wireOp",VERTEX,"E549");
            var Q9;
            Q9=sQuery(id+"F2.wireOp",VERTEX,"E514");
            var Q10;
            Q10=sQuery(id+"F2.wireOp",VERTEX,"E479");
            var Q11;
            Q11=sQuery(id+"F2.wireOp",VERTEX,"E445");
            var Q12;
            Q12=sQuery(id+"F2.wireOp",VERTEX,"E391");
            var Q13;
            Q13=sQuery(id+"F2.wireOp",VERTEX,"E765");
            var Q14;
            Q14=sQuery(id+"F2.wireOp",VERTEX,"E903");
            var Q15;
            Q15=sQuery(id+"F2.wireOp",VERTEX,"E881");
            var Q16;
            Q16=makeQuery(id+"F1.opRevolve","SWEPT_BODY",BODY,{"disambiguationData":[OSD([sQuery(id+"F0.wireOp",EDGE,"E0"),sQuery(id+"F0.wireOp",EDGE,"E1"),sQuery(id+"F0.wireOp",EDGE,"E2"),sQuery(id+"F0.wireOp",EDGE,"E3")])]});
            hole(context, id + "F18", {"style" : HoleStyle.SIMPLE, "endStyle" : HoleEndStyle.THROUGH, "holeDiameter" : 1.2 * mm, "tappedDepth" : 12 * mm, "tapClearance" : 3, "locations" : qUnion([Q0, Q1, Q2, Q3, Q4, Q5, Q6, Q7, Q8, Q9, Q10, Q11, Q12, Q13, Q14, Q15]), "scope" : qUnion([Q16])});
        }
        {
            var Q0;
            Q0=sQuery(id+"F2.wireOp",VERTEX,"E825");
            var Q1;
            Q1=sQuery(id+"F2.wireOp",VERTEX,"E751");
            var Q2;
            Q2=sQuery(id+"F2.wireOp",VERTEX,"E786");
            var Q3;
            Q3=sQuery(id+"F2.wireOp",VERTEX,"E696");
            var Q4;
            Q4=sQuery(id+"F2.wireOp",VERTEX,"E666");
            var Q5;
            Q5=sQuery(id+"F2.wireOp",VERTEX,"E628");
            var Q6;
            Q6=sQuery(id+"F2.wireOp",VERTEX,"E598");
            var Q7;
            Q7=sQuery(id+"F2.wireOp",VERTEX,"E566");
            var Q8;
            Q8=sQuery(id+"F2.wireOp",VERTEX,"E534");
            var Q9;
            Q9=sQuery(id+"F2.wireOp",VERTEX,"E497");
            var Q10;
            Q10=sQuery(id+"F2.wireOp",VERTEX,"E463");
            var Q11;
            Q11=sQuery(id+"F2.wireOp",VERTEX,"E425");
            var Q12;
            Q12=sQuery(id+"F2.wireOp",VERTEX,"E407");
            var Q13;
            Q13=sQuery(id+"F2.wireOp",VERTEX,"E907");
            var Q14;
            Q14=sQuery(id+"F2.wireOp",VERTEX,"E905");
            var Q15;
            Q15=sQuery(id+"F2.wireOp",VERTEX,"E860");
            var Q16;
            Q16=makeQuery(id+"F1.opRevolve","SWEPT_BODY",BODY,{"disambiguationData":[OSD([sQuery(id+"F0.wireOp",EDGE,"E0"),sQuery(id+"F0.wireOp",EDGE,"E1"),sQuery(id+"F0.wireOp",EDGE,"E2"),sQuery(id+"F0.wireOp",EDGE,"E3")])]});
            hole(context, id + "F9", {"style" : HoleStyle.SIMPLE, "endStyle" : HoleEndStyle.THROUGH, "holeDiameter" : 1.2 * mm, "tappedDepth" : 12 * mm, "tapClearance" : 3, "locations" : qUnion([Q0, Q1, Q2, Q3, Q4, Q5, Q6, Q7, Q8, Q9, Q10, Q11, Q12, Q13, Q14, Q15]), "scope" : qUnion([Q16])});
        }
        {
            var Q0;
            Q0=sQuery(id+"F2.wireOp",VERTEX,"E833");
            var Q1;
            Q1=sQuery(id+"F2.wireOp",VERTEX,"E810");
            var Q2;
            Q2=sQuery(id+"F2.wireOp",VERTEX,"E736");
            var Q3;
            Q3=sQuery(id+"F2.wireOp",VERTEX,"E719");
            var Q4;
            Q4=sQuery(id+"F2.wireOp",VERTEX,"E685");
            var Q5;
            Q5=sQuery(id+"F2.wireOp",VERTEX,"E651");
            var Q6;
            Q6=sQuery(id+"F2.wireOp",VERTEX,"E618");
            var Q7;
            Q7=sQuery(id+"F2.wireOp",VERTEX,"E575");
            var Q8;
            Q8=sQuery(id+"F2.wireOp",VERTEX,"E552");
            var Q9;
            Q9=sQuery(id+"F2.wireOp",VERTEX,"E511");
            var Q10;
            Q10=sQuery(id+"F2.wireOp",VERTEX,"E482");
            var Q11;
            Q11=sQuery(id+"F2.wireOp",VERTEX,"E448");
            var Q12;
            Q12=sQuery(id+"F2.wireOp",VERTEX,"E388");
            var Q13;
            Q13=sQuery(id+"F2.wireOp",VERTEX,"E762");
            var Q14;
            Q14=sQuery(id+"F2.wireOp",VERTEX,"E912");
            var Q15;
            Q15=sQuery(id+"F2.wireOp",VERTEX,"E884");
            var Q16;
            Q16=makeQuery(id+"F1.opRevolve","SWEPT_BODY",BODY,{"disambiguationData":[OSD([sQuery(id+"F0.wireOp",EDGE,"E0"),sQuery(id+"F0.wireOp",EDGE,"E1"),sQuery(id+"F0.wireOp",EDGE,"E2"),sQuery(id+"F0.wireOp",EDGE,"E3")])]});
            hole(context, id + "F10", {"style" : HoleStyle.SIMPLE, "endStyle" : HoleEndStyle.THROUGH, "holeDiameter" : 1.2 * mm, "tappedDepth" : 12 * mm, "tapClearance" : 3, "locations" : qUnion([Q0, Q1, Q2, Q3, Q4, Q5, Q6, Q7, Q8, Q9, Q10, Q11, Q12, Q13, Q14, Q15]), "scope" : qUnion([Q16])});
        }
        {
            var Q0;
            Q0=sQuery(id+"F2.wireOp",VERTEX,"E863");
            var Q1;
            Q1=sQuery(id+"F2.wireOp",VERTEX,"E828");
            var Q2;
            Q2=sQuery(id+"F2.wireOp",VERTEX,"E754");
            var Q3;
            Q3=sQuery(id+"F2.wireOp",VERTEX,"E789");
            var Q4;
            Q4=sQuery(id+"F2.wireOp",VERTEX,"E693");
            var Q5;
            Q5=sQuery(id+"F2.wireOp",VERTEX,"E669");
            var Q6;
            Q6=sQuery(id+"F2.wireOp",VERTEX,"E625");
            var Q7;
            Q7=sQuery(id+"F2.wireOp",VERTEX,"E601");
            var Q8;
            Q8=sQuery(id+"F2.wireOp",VERTEX,"E569");
            var Q9;
            Q9=sQuery(id+"F2.wireOp",VERTEX,"E537");
            var Q10;
            Q10=sQuery(id+"F2.wireOp",VERTEX,"E500");
            var Q11;
            Q11=sQuery(id+"F2.wireOp",VERTEX,"E466");
            var Q12;
            Q12=sQuery(id+"F2.wireOp",VERTEX,"E422");
            var Q13;
            Q13=sQuery(id+"F2.wireOp",VERTEX,"E404");
            var Q14;
            Q14=sQuery(id+"F2.wireOp",VERTEX,"E914");
            var Q15;
            Q15=sQuery(id+"F2.wireOp",VERTEX,"E916");
            var Q16;
            Q16=makeQuery(id+"F1.opRevolve","SWEPT_BODY",BODY,{"disambiguationData":[OSD([sQuery(id+"F0.wireOp",EDGE,"E0"),sQuery(id+"F0.wireOp",EDGE,"E1"),sQuery(id+"F0.wireOp",EDGE,"E2"),sQuery(id+"F0.wireOp",EDGE,"E3")])]});
            hole(context, id + "F11", {"style" : HoleStyle.SIMPLE, "endStyle" : HoleEndStyle.THROUGH, "holeDiameter" : 1.2 * mm, "tappedDepth" : 12 * mm, "tapClearance" : 3, "locations" : qUnion([Q0, Q1, Q2, Q3, Q4, Q5, Q6, Q7, Q8, Q9, Q10, Q11, Q12, Q13, Q14, Q15]), "scope" : qUnion([Q16])});
        }
        {
            var Q0;
            Q0=sQuery(id+"F2.wireOp",VERTEX,"E836");
            var Q1;
            Q1=sQuery(id+"F2.wireOp",VERTEX,"E813");
            var Q2;
            Q2=sQuery(id+"F2.wireOp",VERTEX,"E739");
            var Q3;
            Q3=sQuery(id+"F2.wireOp",VERTEX,"E722");
            var Q4;
            Q4=sQuery(id+"F2.wireOp",VERTEX,"E688");
            var Q5;
            Q5=sQuery(id+"F2.wireOp",VERTEX,"E654");
            var Q6;
            Q6=sQuery(id+"F2.wireOp",VERTEX,"E621");
            var Q7;
            Q7=sQuery(id+"F2.wireOp",VERTEX,"E572");
            var Q8;
            Q8=sQuery(id+"F2.wireOp",VERTEX,"E555");
            var Q9;
            Q9=sQuery(id+"F2.wireOp",VERTEX,"E508");
            var Q10;
            Q10=sQuery(id+"F2.wireOp",VERTEX,"E485");
            var Q11;
            Q11=sQuery(id+"F2.wireOp",VERTEX,"E451");
            var Q12;
            Q12=sQuery(id+"F2.wireOp",VERTEX,"E385");
            var Q13;
            Q13=sQuery(id+"F2.wireOp",VERTEX,"E759");
            var Q14;
            Q14=sQuery(id+"F2.wireOp",VERTEX,"E921");
            var Q15;
            Q15=sQuery(id+"F2.wireOp",VERTEX,"E887");
            var Q16;
            Q16=makeQuery(id+"F1.opRevolve","SWEPT_BODY",BODY,{"disambiguationData":[OSD([sQuery(id+"F0.wireOp",EDGE,"E0"),sQuery(id+"F0.wireOp",EDGE,"E1"),sQuery(id+"F0.wireOp",EDGE,"E2"),sQuery(id+"F0.wireOp",EDGE,"E3")])]});
            hole(context, id + "F19", {"style" : HoleStyle.SIMPLE, "endStyle" : HoleEndStyle.THROUGH, "holeDiameter" : 1.2 * mm, "tappedDepth" : 12 * mm, "tapClearance" : 3, "locations" : qUnion([Q0, Q1, Q2, Q3, Q4, Q5, Q6, Q7, Q8, Q9, Q10, Q11, Q12, Q13, Q14, Q15]), "scope" : qUnion([Q16])});
        }
        {
            var Q0;
            Q0=sQuery(id+"F2.wireOp",VERTEX,"E59.end");
            var Q1;
            Q1=sQuery(id+"F2.wireOp",VERTEX,"E831");
            var Q2;
            Q2=sQuery(id+"F2.wireOp",VERTEX,"E61.end");
            var Q3;
            Q3=sQuery(id+"F2.wireOp",VERTEX,"E62.end");
            var Q4;
            Q4=sQuery(id+"F2.wireOp",VERTEX,"E690");
            var Q5;
            Q5=sQuery(id+"F2.wireOp",VERTEX,"E672");
            var Q6;
            Q6=sQuery(id+"F2.wireOp",VERTEX,"E622");
            var Q7;
            Q7=sQuery(id+"F2.wireOp",VERTEX,"E50.end");
            var Q8;
            Q8=sQuery(id+"F2.wireOp",VERTEX,"E51.end");
            var Q9;
            Q9=sQuery(id+"F2.wireOp",VERTEX,"E505");
            var Q10;
            Q10=sQuery(id+"F2.wireOp",VERTEX,"E503");
            var Q11;
            Q11=sQuery(id+"F2.wireOp",VERTEX,"E469");
            var Q12;
            Q12=sQuery(id+"F2.wireOp",VERTEX,"E55.end");
            var Q13;
            Q13=sQuery(id+"F2.wireOp",VERTEX,"E401");
            var Q14;
            Q14=sQuery(id+"F2.wireOp",VERTEX,"E926");
            var Q15;
            Q15=sQuery(id+"F2.wireOp",VERTEX,"E905");
            var Q16;
            Q16=sQuery(id+"F2.wireOp",VERTEX,"E919");
            var Q17;
            Q17=makeQuery(id+"F1.opRevolve","SWEPT_BODY",BODY,{"disambiguationData":[OSD([sQuery(id+"F0.wireOp",EDGE,"E0"),sQuery(id+"F0.wireOp",EDGE,"E1"),sQuery(id+"F0.wireOp",EDGE,"E2"),sQuery(id+"F0.wireOp",EDGE,"E3")])]});
            hole(context, id + "F20", {"style" : HoleStyle.SIMPLE, "endStyle" : HoleEndStyle.THROUGH, "holeDiameter" : 1.2 * mm, "tappedDepth" : 12 * mm, "tapClearance" : 3, "locations" : qUnion([Q0, Q1, Q2, Q3, Q4, Q5, Q6, Q7, Q8, Q9, Q10, Q11, Q12, Q13, Q14, Q15, Q16]), "scope" : qUnion([Q17])});
        }
    });
